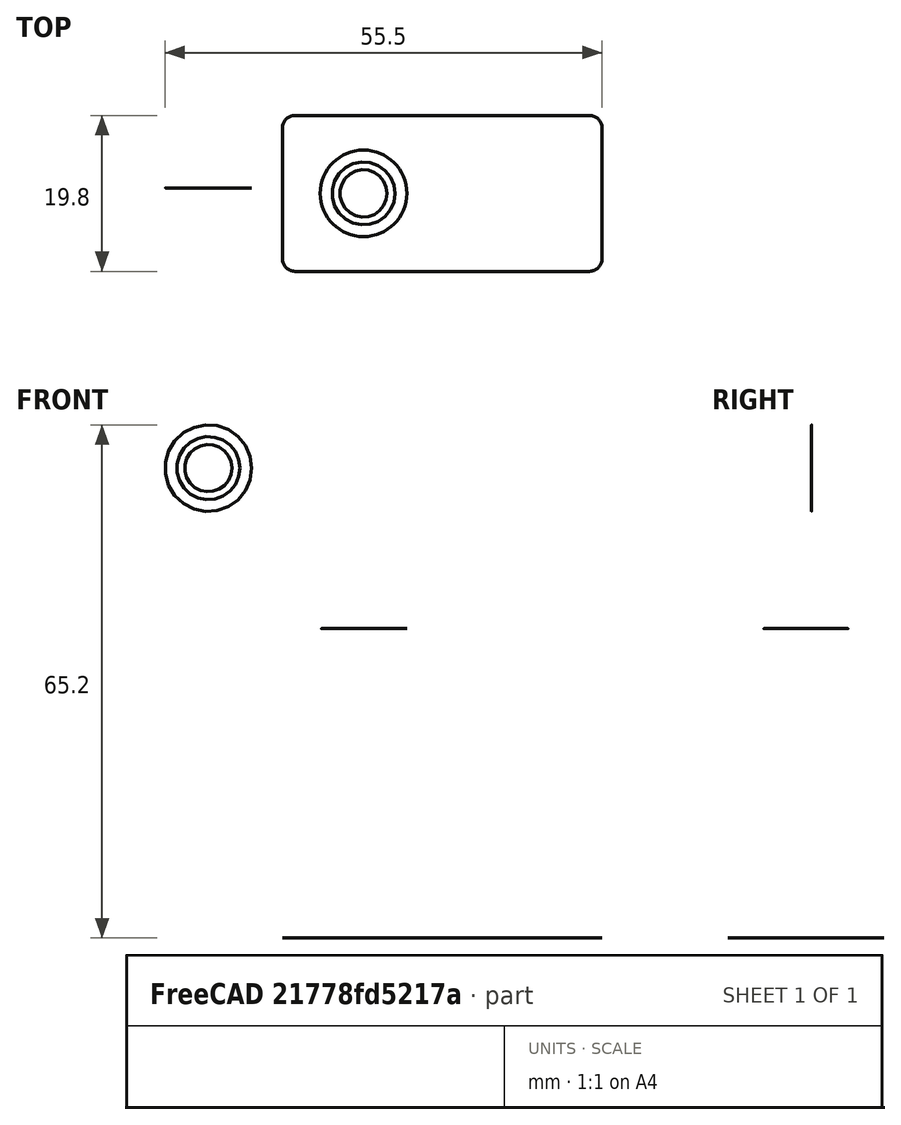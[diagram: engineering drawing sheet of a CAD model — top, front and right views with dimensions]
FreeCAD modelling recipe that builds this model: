
FCSTD DOCUMENT  (FreeCAD 2023.1102R14555 (Git shallow))
Label: Final_Assembly
License: All rights reserved
LicenseURL: https://en.wikipedia.org/wiki/All_rights_reserved
objects: App::FeaturePython×10, Part::FeaturePython×7, App::Link×3
note: 6 computed .brp shape members not serialized (recipe doc carries the construction recipe); baked Part::Feature solids carry a one-line shape summary decoded from their .brp
EXTERNAL_REF file=Base_Plate.FCStd obj=Assembly
EXTERNAL_REF file=Top_Base.FCStd obj=Assembly
EXTERNAL_REF file=Camera_Base.FCStd obj=Assembly

FEATURE [App::Link] Link  label="Link(Base_Plate_Assembly)"
  AutoLinkLabel = true
  AutoPlacement = true
  LinkedObject = -> <external Base_Plate.FCStd>#Assembly
  SyncGroupVisibility = false
  TreeRank = 1
  _LinkVersion = 1
FEATURE [App::Link] Link001  label="Link001(Top_Base_Assembly)"
  AutoLinkLabel = true
  AutoPlacement = true
  LinkPlacement = pos=(0,0,8.3) rot=(0,0,1;1.5708rad)
  LinkedObject = -> <external Top_Base.FCStd>#Assembly
  Placement = pos=(0,0,8.3) rot=(0,0,1;1.5708rad)
  SyncGroupVisibility = false
  TreeRank = 2
  _LinkVersion = 1
FEATURE [App::Link] Link002  label="Link002(Camera_Base_Assembly)"
  AutoLinkLabel = true
  AutoPlacement = true
  LinkPlacement = pos=(-19.7,-5.8,22.2) rot=(-1.2e-05,-1.2e-05,1;1.5708rad)
  LinkedObject = -> <external Camera_Base.FCStd>#Assembly
  Placement = pos=(-19.7,-5.8,22.2) rot=(-1.2e-05,-1.2e-05,1;1.5708rad)
  SyncGroupVisibility = false
  TreeRank = 16
  _LinkVersion = 1
FEATURE [Part::FeaturePython] Parts  # WARN: FeaturePython — macro-defined, semantics opaque (R4)
  Group = -> [Link,Link001,Link002]
  GroupMode = 0
  InvalidShape = false
  TreeRank = 0
  ValidateShape = false
  _LinkVersion = 1
FEATURE [Part::FeaturePython] Assembly  # WARN: FeaturePython — macro-defined, semantics opaque (R4)
  AutoRelax = true
  BuildShape = 0
  Freeze = false
  Group = -> [Constraints,Elements,Parts]
  InvalidShape = false
  TreeRank = 0
  ValidateShape = false
  Verbose = false
  _LinkVersion = 1
  _SolverType = 1
  _Version = 1
FEATURE [App::FeaturePython] Constraints  # WARN: FeaturePython — macro-defined, semantics opaque (R4)
  Group = -> [Constraint,Constraint001,Constraint002]
  TreeRank = 0
  _LinkVersion = 1
  _Version = 1
FEATURE [App::FeaturePython] Elements  # WARN: FeaturePython — macro-defined, semantics opaque (R4)
  Group = -> [_Element,_Element001,_Element002,_Element003,_Element004]
  TreeRank = 0
  _LinkVersion = 1
FEATURE [App::FeaturePython] Constraint  label="Locked"  # WARN: FeaturePython — macro-defined, semantics opaque (R4)
  Disabled = false
  Group = -> [ElementLink]
  TreeRank = 6
  _ConstraintType = 0
  _LinkVersion = 1
  _Parent = -> Constraints
FEATURE [App::FeaturePython] ElementLink  label="_Element"  # link proxy (typed FeaturePython)
  LinkTransform = true
  LinkedObject = -> _Element
  TreeRank = 4
  _LinkVersion = 1
  _Parent = -> Constraint
FEATURE [Part::FeaturePython] _Element  # link proxy (typed FeaturePython)
  Detach = false
  InvalidShape = false
  LinkTransform = true
  LinkedObject = -> Link [1.$Element.]
  TreeRank = 7
  ValidateShape = false
  _LinkVersion = 1
  _Parent = -> Elements
FEATURE [App::FeaturePython] Constraint001  label="PlaneCoincident"  # WARN: FeaturePython — macro-defined, semantics opaque (R4)
  Angle = 0
  AnglePitch = 0
  AngleRoll = 0
  Cascade = false
  Disabled = false
  Group = -> [ElementLink001,ElementLink002]
  LockAngle = true
  Multiply = false
  OffsetX = 0
  OffsetY = 0
  TreeRank = 13
  _ConstraintType = 35
  _LinkVersion = 1
  _Parent = -> Constraints
FEATURE [App::FeaturePython] ElementLink001  label="_Element001"  # link proxy (typed FeaturePython)
  LinkTransform = true
  LinkedObject = -> _Element001
  TreeRank = 9
  _LinkVersion = 1
  _Parent = -> Constraint001
FEATURE [Part::FeaturePython] _Element001  # link proxy (typed FeaturePython)
  Detach = false
  InvalidShape = false
  LinkTransform = true
  LinkedObject = -> Link [1.$Element001.]
  TreeRank = 14
  ValidateShape = false
  _LinkVersion = 1
  _Parent = -> Elements
FEATURE [App::FeaturePython] ElementLink002  label="_Element002"  # link proxy (typed FeaturePython)
  LinkTransform = true
  LinkedObject = -> _Element002
  TreeRank = 11
  _LinkVersion = 1
  _Parent = -> Constraint001
FEATURE [Part::FeaturePython] _Element002  # link proxy (typed FeaturePython)
  Detach = false
  InvalidShape = false
  LinkTransform = true
  LinkedObject = -> Link001 [1.$_Element.]
  TreeRank = 15
  ValidateShape = false
  _LinkVersion = 1
  _Parent = -> Elements
FEATURE [App::FeaturePython] Constraint002  label="PlaneCoincident001"  # WARN: FeaturePython — macro-defined, semantics opaque (R4)
  Angle = 0
  AnglePitch = 0
  AngleRoll = 18
  Cascade = false
  Disabled = false
  Group = -> [ElementLink003,ElementLink004]
  LockAngle = false
  Multiply = false
  OffsetX = 0
  OffsetY = 0
  TreeRank = 22
  _ConstraintType = 35
  _LinkVersion = 1
  _Parent = -> Constraints
FEATURE [App::FeaturePython] ElementLink003  label="Servo_Gear_Base@Link001(Top_Base_Assembly)@"  # link proxy (typed FeaturePython)
  LinkTransform = true
  LinkedObject = -> _Element003
  TreeRank = 18
  _LinkVersion = 1
  _Parent = -> Constraint002
FEATURE [Part::FeaturePython] _Element003  label="Servo_Gear_Base@Link001(Top_Base_Assembly)@"  # link proxy (typed FeaturePython)
  Detach = false
  InvalidShape = false
  LinkTransform = true
  LinkedObject = -> Link001 [1.$Servo_Gear_Base.]
  TreeRank = 23
  ValidateShape = false
  _LinkVersion = 1
  _Parent = -> Elements
FEATURE [App::FeaturePython] ElementLink004  label="Horn_Base@Link002(Camera_Base_Assembly)@"  # link proxy (typed FeaturePython)
  LinkTransform = true
  LinkedObject = -> _Element004
  TreeRank = 20
  _LinkVersion = 1
  _Parent = -> Constraint002
FEATURE [Part::FeaturePython] _Element004  label="Horn_Base@Link002(Camera_Base_Assembly)@"  # link proxy (typed FeaturePython)
  Detach = false
  InvalidShape = false
  LinkTransform = true
  LinkedObject = -> Link002 [1.$Horn_Base.]
  TreeRank = 24
  ValidateShape = false
  _LinkVersion = 1
  _Parent = -> Elements

RESOLVED EXTERNAL PARTS (link-assembly join: the EXTERNAL_REF files above that resolve inside this repo's crawl, each included once):
---- part Base_Plate.FCStd = doc fcstd_8688ca83c108 ----
FCSTD DOCUMENT  (FreeCAD 2023.1102R14555 (Git shallow))
Label: Base_Plate
License: All rights reserved
LicenseURL: https://en.wikipedia.org/wiki/All_rights_reserved
objects: Sketcher::SketchObject×11, Part::FeaturePython×7, App::FeaturePython×7, PartDesign::Pad×6, PartDesign::Pocket×6, PartDesign::Plane×5, PartDesign::Fillet×3, PartDesign::SubShapeBinder×2, PartDesign::Body×2, App::Part×2, App::Link×1
note: 82 computed .brp shape members not serialized (recipe doc carries the construction recipe); baked Part::Feature solids carry a one-line shape summary decoded from their .brp
EXTERNAL_REF file=Hitec_D625MW.FCStd obj=Part
EXTERNAL_REF file=Final_Assembly.FCStd obj=Assembly

FEATURE [App::Link] Link  label="Link(Hitec_D625MW)"
  AutoLinkLabel = true
  AutoPlacement = true
  LinkPlacement = pos=(-10.3,-9.9,-37.5) rot=(0,0,1;0rad)
  LinkedObject = -> <external Hitec_D625MW.FCStd>#Part
  Placement = pos=(-10.3,-9.9,-37.5) rot=(0,0,1;0rad)
  SyncGroupVisibility = false
  TreeRank = 1
  _LinkVersion = 1
FEATURE [Sketcher::SketchObject] Sketch
  ArcFitTolerance = 1e-06
  AttachmentSupport = -> [XY_Plane]
  ExternalBSplineMaxDegree = 5
  ExternalBSplineTolerance = 0.0001
  FullyConstrained = true
  InternalTolerance = 1e-06
  InvalidShape = false
  MakeInternals = false
  MapMode = 5
  Support = -> [XY_Plane]
  TreeRank = 21
  ValidateShape = false
  sketch-geometry (6):
    g0: LineSegment StartX=-40 StartY=-40 StartZ=0 EndX=-40 EndY=40 EndZ=0
    g1: LineSegment StartX=-40 StartY=40 StartZ=0 EndX=40 EndY=40 EndZ=0
    g2: LineSegment StartX=40 StartY=40 StartZ=0 EndX=40 EndY=-40 EndZ=0
    g3: LineSegment StartX=40 StartY=-40 StartZ=0 EndX=-40 EndY=-40 EndZ=0
    g4: GeomPoint [constr] X=0 Y=0 Z=0
    g5: Circle CenterX=0 CenterY=0 CenterZ=0 NormalX=0 NormalY=0 NormalZ=1 AngleXU=0 Radius=10
  constraints (14):
    c: Coincident(g0,g1)
    c: Coincident(g1,g2)
    c: Coincident(g2,g3)
    c: Coincident(g3,g0)
    c: Horizontal(g1)
    c: Horizontal(g3)
    c: Vertical(g0)
    c: Vertical(g2)
    c: Symmetric(g1,g0,g4)
    c: Coincident(g4,g-1)
    c: Equal(g1,g2)
    c: Distance(g1) = 80
    c: Diameter(g5) = 20
    c: Coincident(g5,g4)
FEATURE [PartDesign::Pad] Pad
  AddSubType = 0
  AlongSketchNormal = false
  AutoTaperInnerAngle = true
  CheckUpToFaceLimits = true
  ClaimChildren = false
  Direction = (0,0,1)
  Fit = 0
  FitJoin = 0
  InnerFit = 0
  InnerFitJoin = 0
  InvalidShape = false
  Length = 4
  Length2 = 10
  Linearize = true
  NewSolid = false
  Profile = -> Sketch
  ReferenceAxis = -> Sketch [N_Axis]
  Refine = true
  Suppress = false
  TaperInnerAngle = 0
  TaperInnerAngleRev = 0
  TreeRank = 22
  Type = 0
  ValidateShape = true
  _ProfileBasedVersion = 1
FEATURE [PartDesign::Fillet] Fillet
  AddSubType = 0
  Base = -> Pad [Edge1,Edge8,Edge5,Edge2]
  BaseFeature = -> Pad
  InvalidShape = false
  NewSolid = false
  Radius = 4
  Refine = true
  SupportTransform = false
  Suppress = false
  TreeRank = 23
  UseAllEdges = false
  ValidateShape = true
FEATURE [PartDesign::SubShapeBinder] Binder  label="Binder(*Hitec_D625MW)"
  BindCopyOnChange = 0
  BindMode = 0
  ClaimChildren = false
  Context = -> Assembly [Parts.Part.Body.Binder.]
  EdgeTolerance = 1e-06
  FillStyle = 0
  Fuse = false
  InvalidShape = false
  MakeFace = true
  MergeEdges = true
  OffsetFill = false
  OffsetIntersection = false
  OffsetJoinType = 0
  OffsetOpenResult = false
  Outline = false
  PartialLoad = false
  Relative = true
  SplitEdges = false
  Support = -> [Link]
  TightBound = false
  TreeRank = 39
  ValidateShape = false
  _Version = 8
FEATURE [Sketcher::SketchObject] Sketch001
  ArcFitTolerance = 1e-06
  AttachmentSupport = -> [Fillet]
  ExternalBSplineMaxDegree = 5
  ExternalBSplineTolerance = 0.0001
  ExternalGeometry = -> [Binder]
  FullyConstrained = true
  InternalTolerance = 1e-06
  InvalidShape = false
  MakeInternals = false
  MapMode = 5
  Placement = pos=(0,0,0) rot=(1,0,0;3.14159rad)
  Support = -> [Fillet]
  TreeRank = 38
  ValidateShape = false
  sketch-geometry (10):
    g0: LineSegment StartX=-17.3 StartY=11.9 StartZ=0 EndX=-10.8 EndY=11.9 EndZ=0
    g1: LineSegment StartX=-10.8 StartY=11.9 StartZ=0 EndX=-10.8 EndY=-11.9 EndZ=0
    g2: LineSegment StartX=-10.8 StartY=-11.9 StartZ=0 EndX=-17.3 EndY=-11.9 EndZ=0
    g3: LineSegment StartX=-17.3 StartY=-11.9 StartZ=0 EndX=-17.3 EndY=11.9 EndZ=0
    g4: LineSegment StartX=30.8 StartY=11.9 StartZ=0 EndX=37.3 EndY=11.9 EndZ=0
    g5: LineSegment StartX=37.3 StartY=11.9 StartZ=0 EndX=37.3 EndY=-11.9 EndZ=0
    g6: LineSegment StartX=37.3 StartY=-11.9 StartZ=0 EndX=30.8 EndY=-11.9 EndZ=0
    g7: LineSegment StartX=30.8 StartY=-11.9 StartZ=0 EndX=30.8 EndY=11.9 EndZ=0
    g8: LineSegment [constr] StartX=-15.2 StartY=9.9 StartZ=0 EndX=-15.2 EndY=11.9 EndZ=0
    g9: LineSegment [constr] StartX=-15.2 StartY=-9.9 StartZ=0 EndX=-15.2 EndY=-11.9 EndZ=0
  constraints (30):
    c: Coincident(g0,g1)
    c: Coincident(g1,g2)
    c: Coincident(g2,g3)
    c: Coincident(g3,g0)
    c: Horizontal(g0)
    c: Horizontal(g2)
    c: Vertical(g1)
    c: Vertical(g3)
    c: Coincident(g4,g5)
    c: Coincident(g5,g6)
    c: Coincident(g6,g7)
    c: Coincident(g7,g4)
    c: Horizontal(g4)
    c: Horizontal(g6)
    c: Vertical(g5)
    c: Vertical(g7)
    c: Equal(g1,g7)
    c: Equal(g0,g4)
    c: Distance(g-10,g1) = 0.5
    c: Distance(g-9,g7) = 0.5
    c: Distance(g-4,g3) = 0.5
    c: Horizontal(g4,g0)
    c: Coincident(g8,g-5)
    c: PointOnObject(g8,g0)
    c: Vertical(g8)
    c: Coincident(g9,g-3)
    c: PointOnObject(g9,g2)
    c: Vertical(g9)
    c: Equal(g9,g8)
    c: Distance(g8) = 2
FEATURE [PartDesign::Pad] Pad001
  AddSubType = 0
  AlongSketchNormal = false
  AutoTaperInnerAngle = true
  BaseFeature = -> Fillet
  CheckUpToFaceLimits = true
  ClaimChildren = false
  Direction = (0,0,-1)
  Fit = 0
  FitJoin = 0
  InnerFit = 0
  InnerFitJoin = 0
  InvalidShape = false
  Length = 10
  Length2 = 10
  Linearize = true
  NewSolid = false
  Profile = -> Sketch001
  ReferenceAxis = -> Sketch001 [N_Axis]
  Refine = true
  Suppress = false
  TaperInnerAngle = 0
  TaperInnerAngleRev = 0
  TreeRank = 40
  Type = 3
  UpToFace = -> Binder [Face2]
  ValidateShape = true
  _ProfileBasedVersion = 1
FEATURE [PartDesign::Plane] DatumPlane
  AttachmentSupport = -> [Pad001]
  InvalidShape = false
  Length = 80
  MapMode = 45
  MinimumLength = 10
  MinimumWidth = 10
  Placement = pos=(10,-1.98471e-11,-8) rot=(-0.707107,0.707107,0;3.14159rad)
  ResizeMode = 0
  Support = -> [Pad001]
  TreeRank = 41
  ValidateShape = false
  Width = 80
FEATURE [Sketcher::SketchObject] Sketch002
  ArcFitTolerance = 1e-06
  AttachmentSupport = -> [DatumPlane]
  ExternalBSplineMaxDegree = 5
  ExternalBSplineTolerance = 0.0001
  ExternalGeometry = -> [Binder,Pad001]
  FullyConstrained = true
  InternalTolerance = 1e-06
  InvalidShape = false
  MakeInternals = false
  MapMode = 5
  Placement = pos=(10,-1.98471e-11,-8) rot=(-0.707107,0.707107,0;3.14159rad)
  Support = -> [DatumPlane]
  TreeRank = 42
  ValidateShape = false
  sketch-geometry (8):
    g0: LineSegment StartX=-0.7 StartY=-20.8 StartZ=0 EndX=0.7 EndY=-20.8 EndZ=0
    g1: LineSegment StartX=0.7 StartY=-20.8 StartZ=0 EndX=0.7 EndY=-27.3 EndZ=0
    g2: LineSegment StartX=0.7 StartY=-27.3 StartZ=0 EndX=-0.7 EndY=-27.3 EndZ=0
    g3: LineSegment StartX=-0.7 StartY=-27.3 StartZ=0 EndX=-0.7 EndY=-20.8 EndZ=0
    g4: LineSegment StartX=0.7 StartY=20.8 StartZ=0 EndX=-0.7 EndY=20.8 EndZ=0
    g5: LineSegment StartX=-0.7 StartY=20.8 StartZ=0 EndX=-0.7 EndY=27.3 EndZ=0
    g6: LineSegment StartX=-0.7 StartY=27.3 StartZ=0 EndX=0.7 EndY=27.3 EndZ=0
    g7: LineSegment StartX=0.7 StartY=27.3 StartZ=0 EndX=0.7 EndY=20.8 EndZ=0
  constraints (22):
    c: Coincident(g0,g1)
    c: Coincident(g1,g2)
    c: Coincident(g2,g3)
    c: Coincident(g3,g0)
    c: Horizontal(g2)
    c: Vertical(g1)
    c: Vertical(g3)
    c: PointOnObject(g0,g-8)
    c: PointOnObject(g1,g-7)
    c: Symmetric(g0,g0,g-2)
    c: Distance(g0,g-6) = 0.1
    c: Coincident(g4,g5)
    c: Coincident(g5,g6)
    c: Coincident(g6,g7)
    c: Coincident(g7,g4)
    c: Horizontal(g6)
    c: Vertical(g5)
    c: Vertical(g7)
    c: PointOnObject(g4,g-9)
    c: PointOnObject(g5,g-10)
    c: Symmetric(g4,g4,g-2)
    c: Distance(g4,g-4) = 0.1
FEATURE [PartDesign::Pocket] Pocket
  AddSubType = 1
  AlongSketchNormal = false
  AutoTaperInnerAngle = true
  BaseFeature = -> Pad001
  CheckUpToFaceLimits = true
  ClaimChildren = false
  Direction = (0,0,1)
  Fit = 0
  FitJoin = 0
  InnerFit = 0
  InnerFitJoin = 0
  InvalidShape = false
  Length = 2.5
  Length2 = 10
  Linearize = true
  NewSolid = false
  Profile = -> Sketch002
  ReferenceAxis = -> Sketch002 [N_Axis]
  Refine = true
  Suppress = false
  TaperInnerAngle = 0
  TaperInnerAngleRev = 0
  TreeRank = 43
  Type = 0
  ValidateShape = true
  _ProfileBasedVersion = 1
  _Version = 1
FEATURE [Sketcher::SketchObject] Sketch003
  ArcFitTolerance = 1e-06
  AttachmentSupport = -> [DatumPlane]
  ExternalBSplineMaxDegree = 5
  ExternalBSplineTolerance = 0.0001
  ExternalGeometry = -> [Pocket,Binder]
  FullyConstrained = true
  InternalTolerance = 1e-06
  InvalidShape = false
  MakeInternals = false
  MapMode = 5
  Placement = pos=(10,-1.98471e-11,-8) rot=(-0.707107,0.707107,0;3.14159rad)
  Support = -> [DatumPlane]
  TreeRank = 44
  ValidateShape = false
  sketch-geometry (16):
    g0: LineSegment StartX=-11.9 StartY=-20.8 StartZ=0 EndX=-10 EndY=-20.8 EndZ=0
    g1: LineSegment StartX=-10 StartY=-20.8 StartZ=0 EndX=-10 EndY=-27.3 EndZ=0
    g2: LineSegment StartX=-10 StartY=-27.3 StartZ=0 EndX=-11.9 EndY=-27.3 EndZ=0
    g3: LineSegment StartX=-11.9 StartY=-27.3 StartZ=0 EndX=-11.9 EndY=-20.8 EndZ=0
    g4: LineSegment StartX=11.9 StartY=-20.8 StartZ=0 EndX=10 EndY=-20.8 EndZ=0
    g5: LineSegment StartX=10 StartY=-20.8 StartZ=0 EndX=10 EndY=-27.3 EndZ=0
    g6: LineSegment StartX=10 StartY=-27.3 StartZ=0 EndX=11.9 EndY=-27.3 EndZ=0
    g7: LineSegment StartX=11.9 StartY=-27.3 StartZ=0 EndX=11.9 EndY=-20.8 EndZ=0
    g8: LineSegment StartX=11.9 StartY=27.3 StartZ=0 EndX=10 EndY=27.3 EndZ=0
    g9: LineSegment StartX=10 StartY=27.3 StartZ=0 EndX=10 EndY=20.8 EndZ=0
    g10: LineSegment StartX=10 StartY=20.8 StartZ=0 EndX=11.9 EndY=20.8 EndZ=0
    g11: LineSegment StartX=11.9 StartY=20.8 StartZ=0 EndX=11.9 EndY=27.3 EndZ=0
    g12: LineSegment StartX=-11.9 StartY=27.3 StartZ=0 EndX=-10 EndY=27.3 EndZ=0
    g13: LineSegment StartX=-10 StartY=27.3 StartZ=0 EndX=-10 EndY=20.8 EndZ=0
    g14: LineSegment StartX=-10 StartY=20.8 StartZ=0 EndX=-11.9 EndY=20.8 EndZ=0
    g15: LineSegment StartX=-11.9 StartY=20.8 StartZ=0 EndX=-11.9 EndY=27.3 EndZ=0
  constraints (40):
    c: Coincident(g0,g1)
    c: Coincident(g1,g2)
    c: Coincident(g2,g3)
    c: Coincident(g3,g0)
    c: Horizontal(g0)
    c: Horizontal(g2)
    c: Vertical(g1)
    c: Coincident(g0,g-6)
    c: Coincident(g2,g-6)
    c: Coincident(g4,g5)
    c: Coincident(g5,g6)
    c: Coincident(g6,g7)
    c: Coincident(g7,g4)
    c: Horizontal(g4)
    c: Horizontal(g6)
    c: Vertical(g5)
    c: Coincident(g4,g-5)
    c: Coincident(g6,g-5)
    c: Coincident(g8,g9)
    c: Coincident(g9,g10)
    c: Coincident(g10,g11)
    c: Coincident(g11,g8)
    c: Horizontal(g8)
    c: Horizontal(g10)
    c: Vertical(g9)
    c: Coincident(g8,g-4)
    c: Coincident(g10,g-4)
    c: Coincident(g12,g13)
    c: Coincident(g13,g14)
    c: Coincident(g14,g15)
    c: Coincident(g15,g12)
    c: Horizontal(g12)
    c: Horizontal(g14)
    c: Vertical(g13)
    c: Coincident(g12,g-3)
    c: Coincident(g14,g-3)
    c: Equal(g12,g8)
    c: Equal(g8,g4)
    c: Equal(g4,g0)
    c: Distance(g-7,g13) = 0.1
FEATURE [PartDesign::Pad] Pad002
  AddSubType = 0
  AlongSketchNormal = false
  AutoTaperInnerAngle = true
  BaseFeature = -> Pocket
  CheckUpToFaceLimits = true
  ClaimChildren = false
  Direction = (0,0,-1)
  Fit = 0
  FitJoin = 0
  InnerFit = 0
  InnerFitJoin = 0
  InvalidShape = false
  Length = 2
  Length2 = 10
  Linearize = true
  NewSolid = false
  Profile = -> Sketch003
  ReferenceAxis = -> Sketch003 [N_Axis]
  Refine = true
  Suppress = false
  TaperInnerAngle = 0
  TaperInnerAngleRev = 0
  TreeRank = 45
  Type = 0
  ValidateShape = true
  _ProfileBasedVersion = 1
FEATURE [Sketcher::SketchObject] Sketch004
  ArcFitTolerance = 1e-06
  AttachmentSupport = -> [Pad002]
  ExternalBSplineMaxDegree = 5
  ExternalBSplineTolerance = 0.0001
  ExternalGeometry = -> [Binder]
  FullyConstrained = true
  InternalTolerance = 1e-06
  InvalidShape = false
  MakeInternals = false
  MapMode = 5
  Placement = pos=(0,0,4) rot=(0,0,1;0rad)
  Support = -> [Pad002]
  TreeRank = 46
  ValidateShape = false
  sketch-geometry (8):
    g0: Circle CenterX=-14.2 CenterY=5.1 CenterZ=0 NormalX=0 NormalY=0 NormalZ=1 AngleXU=0 Radius=2.3
    g1: Circle CenterX=-14.2 CenterY=-5.1 CenterZ=0 NormalX=0 NormalY=0 NormalZ=1 AngleXU=0 Radius=2.3
    g2: Circle CenterX=34.2 CenterY=5.1 CenterZ=0 NormalX=0 NormalY=0 NormalZ=1 AngleXU=0 Radius=2.3
    g3: Circle CenterX=34.2 CenterY=-5.1 CenterZ=0 NormalX=0 NormalY=0 NormalZ=1 AngleXU=0 Radius=2.3
    g4: Circle CenterX=-14.2 CenterY=5.1 CenterZ=0 NormalX=0 NormalY=0 NormalZ=1 AngleXU=0 Radius=3.75
    g5: Circle CenterX=-14.2 CenterY=-5.1 CenterZ=0 NormalX=0 NormalY=0 NormalZ=1 AngleXU=0 Radius=3.75
    g6: Circle CenterX=34.2 CenterY=5.1 CenterZ=0 NormalX=0 NormalY=0 NormalZ=1 AngleXU=0 Radius=3.75
    g7: Circle CenterX=34.2 CenterY=-5.1 CenterZ=0 NormalX=0 NormalY=0 NormalZ=1 AngleXU=0 Radius=3.75
  constraints (16):
    c: Coincident(g0,g-4)
    c: Coincident(g1,g-3)
    c: Coincident(g2,g-6)
    c: Coincident(g3,g-5)
    c: Equal(g2,g3)
    c: Equal(g3,g1)
    c: Equal(g1,g0)
    c: Diameter(g0) = 4.6
    c: Coincident(g4,g0)
    c: Coincident(g5,g1)
    c: Coincident(g6,g2)
    c: Coincident(g7,g3)
    c: Equal(g7,g6)
    c: Equal(g6,g4)
    c: Equal(g4,g5)
    c: Diameter(g5) = 7.5
FEATURE [PartDesign::Pocket] Pocket001
  AddSubType = 1
  AlongSketchNormal = false
  AutoTaperInnerAngle = true
  BaseFeature = -> Pad002
  CheckUpToFaceLimits = true
  ClaimChildren = false
  Direction = (0,0,-1)
  Fit = 0
  FitJoin = 0
  InnerFit = 0
  InnerFitJoin = 0
  InvalidShape = false
  Length = 5
  Length2 = 10
  Linearize = true
  NewSolid = false
  Profile = -> Sketch004 [Edge4,Edge3,Edge2,Edge1]
  ReferenceAxis = -> Sketch004 [N_Axis]
  Refine = true
  Suppress = false
  TaperInnerAngle = 0
  TaperInnerAngleRev = 0
  TreeRank = 47
  Type = 1
  ValidateShape = true
  _ProfileBasedVersion = 1
  _Version = 1
FEATURE [PartDesign::Pocket] Pocket002
  AddSubType = 1
  AlongSketchNormal = false
  AutoTaperInnerAngle = true
  BaseFeature = -> Pocket001
  CheckUpToFaceLimits = true
  ClaimChildren = false
  Direction = (0,0,-1)
  Fit = 0
  FitJoin = 0
  InnerFit = 0
  InnerFitJoin = 0
  InvalidShape = false
  Length = 3
  Length2 = 10
  Linearize = true
  NewSolid = false
  Profile = -> Sketch004 [Edge7,Edge8,Edge6,Edge5]
  ReferenceAxis = -> Sketch004 [N_Axis]
  Refine = true
  Suppress = false
  TaperInnerAngle = 0
  TaperInnerAngleRev = 0
  TreeRank = 48
  Type = 0
  ValidateShape = true
  _ProfileBasedVersion = 1
  _Version = 1
FEATURE [PartDesign::Body] Body
  AutoGroupSolids = false
  ClaimAllChildren = false
  ExportMode = 0
  Group = -> [Sketch,Pad,Fillet,Binder,Sketch001,Pad001,DatumPlane,Sketch002,Pocket,Sketch003,Pad002,Sketch004,Pocket001,Pocket002]
  InvalidShape = false
  Origin = -> Origin001
  Tip = -> Pocket002
  TreeRank = 19
  ValidateShape = false
  _ExportChildren = -> [Pad,Fillet,Binder,Pad001,DatumPlane,Pocket,Pad002,Pocket001,Pocket002]
  _GroupVersion = 1
FEATURE [App::Part] Part  label="Base_Plate"
  ClaimAllChildren = false
  ExportMode = 1
  Group = -> [Body]
  Origin = -> Origin
  TreeRank = 7
  _ExportChildren = -> [Body]
  _GroupVersion = 1
FEATURE [PartDesign::SubShapeBinder] Binder001  label="Binder001(*Hitec_D625MW)"
  BindCopyOnChange = 0
  BindMode = 0
  ClaimChildren = false
  Context = -> <external Final_Assembly.FCStd>#Assembly [Parts.Link.Parts.Part001.Body001.Binder001.]
  EdgeTolerance = 1e-06
  FillStyle = 0
  Fuse = false
  InvalidShape = false
  MakeFace = true
  MergeEdges = true
  OffsetFill = false
  OffsetIntersection = false
  OffsetJoinType = 0
  OffsetOpenResult = false
  Outline = false
  PartialLoad = false
  Relative = true
  SplitEdges = false
  Support = -> [Link]
  TightBound = false
  TreeRank = 68
  ValidateShape = false
  _Version = 8
FEATURE [PartDesign::Plane] DatumPlane001
  AttachmentOffset = pos=(0,0,1) rot=(0,0,1;0rad)
  AttachmentSupport = -> [Binder001]
  InvalidShape = false
  Length = 10
  MapMode = 5
  MinimumLength = 10
  MinimumWidth = 10
  Placement = pos=(0,0,-38.5) rot=(1,0,0;3.14159rad)
  ResizeMode = 0
  Support = -> [Binder001]
  TreeRank = 69
  ValidateShape = false
  Width = 10
FEATURE [Sketcher::SketchObject] Sketch005
  ArcFitTolerance = 1e-06
  AttachmentSupport = -> [DatumPlane001]
  ExternalBSplineMaxDegree = 5
  ExternalBSplineTolerance = 0.0001
  ExternalGeometry = -> [Binder001]
  FullyConstrained = true
  InternalTolerance = 1e-06
  InvalidShape = false
  MakeInternals = false
  MapMode = 5
  Placement = pos=(0,0,-38.5) rot=(1,0,0;3.14159rad)
  Support = -> [DatumPlane001]
  TreeRank = 70
  ValidateShape = false
  sketch-geometry (6):
    g0: LineSegment StartX=-43.7 StartY=-60 StartZ=0 EndX=46.3 EndY=-60 EndZ=0
    g1: LineSegment StartX=46.3 StartY=-60 StartZ=0 EndX=46.3 EndY=30 EndZ=0
    g2: LineSegment StartX=46.3 StartY=30 StartZ=0 EndX=-43.7 EndY=30 EndZ=0
    g3: LineSegment StartX=-43.7 StartY=30 StartZ=0 EndX=-43.7 EndY=-60 EndZ=0
    g4: LineSegment [constr] StartX=-8.7 StartY=9.9 StartZ=0 EndX=-43.7 EndY=9.9 EndZ=0
    g5: LineSegment [constr] StartX=28.7 StartY=9.9 StartZ=0 EndX=46.3 EndY=9.9 EndZ=0
  constraints (18):
    c: Coincident(g0,g1)
    c: Coincident(g1,g2)
    c: Coincident(g2,g3)
    c: Coincident(g3,g0)
    c: Horizontal(g0)
    c: Horizontal(g2)
    c: Vertical(g3)
    c: Equal(g1,g0)
    c: Distance(g1) = 90
    c: Coincident(g4,g-3)
    c: PointOnObject(g4,g3)
    c: Horizontal(g4)
    c: Coincident(g5,g-3)
    c: PointOnObject(g5,g1)
    c: Horizontal(g5)
    c: DistanceY(g-1,g2) = 30
    c: Vertical(g1)
    c: Distance(g4) = 35
FEATURE [PartDesign::Pad] Pad003
  AddSubType = 0
  AlongSketchNormal = false
  AutoTaperInnerAngle = true
  CheckUpToFaceLimits = true
  ClaimChildren = false
  Direction = (0,0,-1)
  Fit = 0
  FitJoin = 0
  InnerFit = 0
  InnerFitJoin = 0
  InvalidShape = false
  Length = 4
  Length2 = 10
  Linearize = true
  NewSolid = false
  Profile = -> Sketch005
  ReferenceAxis = -> Sketch005 [N_Axis]
  Refine = true
  Suppress = false
  TaperInnerAngle = 0
  TaperInnerAngleRev = 0
  TreeRank = 71
  Type = 0
  ValidateShape = true
  _ProfileBasedVersion = 1
FEATURE [Sketcher::SketchObject] Sketch006
  ArcFitTolerance = 1e-06
  AttachmentSupport = -> [Pad003]
  ExternalBSplineMaxDegree = 5
  ExternalBSplineTolerance = 0.0001
  ExternalGeometry = -> [Binder001]
  FullyConstrained = true
  InternalTolerance = 1e-06
  InvalidShape = false
  MakeInternals = false
  MapMode = 5
  Placement = pos=(0,0,-38.5) rot=(0,0,1;0rad)
  Support = -> [Pad003]
  TreeRank = 72
  ValidateShape = false
  sketch-geometry (10):
    g0: LineSegment StartX=31.3 StartY=11.9 StartZ=0 EndX=37.3 EndY=11.9 EndZ=0
    g1: LineSegment StartX=37.3 StartY=11.9 StartZ=0 EndX=37.3 EndY=-11.9 EndZ=0
    g2: LineSegment StartX=37.3 StartY=-11.9 StartZ=0 EndX=31.3 EndY=-11.9 EndZ=0
    g3: LineSegment StartX=31.3 StartY=-11.9 StartZ=0 EndX=31.3 EndY=11.9 EndZ=0
    g4: LineSegment StartX=-11.3 StartY=11.9 StartZ=0 EndX=-17.3 EndY=11.9 EndZ=0
    g5: LineSegment StartX=-17.3 StartY=11.9 StartZ=0 EndX=-17.3 EndY=-11.9 EndZ=0
    g6: LineSegment StartX=-17.3 StartY=-11.9 StartZ=0 EndX=-11.3 EndY=-11.9 EndZ=0
    g7: LineSegment StartX=-11.3 StartY=-11.9 StartZ=0 EndX=-11.3 EndY=11.9 EndZ=0
    g8: LineSegment [constr] StartX=-15.2 StartY=-9.9 StartZ=0 EndX=-15.2 EndY=-11.9 EndZ=0
    g9: LineSegment [constr] StartX=-15.2 StartY=9.9 StartZ=0 EndX=-15.2 EndY=11.9 EndZ=0
  constraints (28):
    c: Coincident(g0,g1)
    c: Coincident(g1,g2)
    c: Coincident(g2,g3)
    c: Coincident(g3,g0)
    c: Horizontal(g0)
    c: Horizontal(g2)
    c: Vertical(g3)
    c: Coincident(g4,g5)
    c: Coincident(g5,g6)
    c: Coincident(g6,g7)
    c: Coincident(g7,g4)
    c: Horizontal(g4)
    c: Horizontal(g6)
    c: Vertical(g7)
    c: Distance(g-3,g3) = 1
    c: Distance(g-4,g7) = 1
    c: Symmetric(g0,g1,g-1)
    c: Symmetric(g5,g4,g-1)
    c: Distance(g-6,g5) = 0.5
    c: Distance(g-5,g1) = 0.5
    c: Equal(g5,g1)
    c: Coincident(g8,g-7)
    c: PointOnObject(g8,g6)
    c: Vertical(g8)
    c: Coincident(g9,g-8)
    c: PointOnObject(g9,g4)
    c: Vertical(g9)
    c: Distance(g8) = 2
FEATURE [PartDesign::Pad] Pad004
  AddSubType = 0
  AlongSketchNormal = false
  AutoTaperInnerAngle = true
  BaseFeature = -> Pad003
  CheckUpToFaceLimits = true
  ClaimChildren = false
  Direction = (0,0,1)
  Fit = 0
  FitJoin = 0
  InnerFit = 0
  InnerFitJoin = 0
  InvalidShape = false
  Length = 10
  Length2 = 10
  Linearize = true
  NewSolid = false
  Profile = -> Sketch006
  ReferenceAxis = -> Sketch006 [N_Axis]
  Refine = true
  Suppress = false
  TaperInnerAngle = 0
  TaperInnerAngleRev = 0
  TreeRank = 73
  Type = 3
  UpToFace = -> Binder001 [Face37]
  ValidateShape = true
  _ProfileBasedVersion = 1
FEATURE [PartDesign::Plane] DatumPlane002
  AttachmentSupport = -> [Pad004]
  InvalidShape = false
  Length = 10
  MapMode = 45
  MinimumLength = 10
  MinimumWidth = 10
  Placement = pos=(10,-6e-16,-10.5) rot=(0,0,1;1.5708rad)
  ResizeMode = 0
  Support = -> [Pad004]
  TreeRank = 74
  ValidateShape = false
  Width = 10
FEATURE [Sketcher::SketchObject] Sketch007
  ArcFitTolerance = 1e-06
  AttachmentSupport = -> [DatumPlane002]
  ExternalBSplineMaxDegree = 5
  ExternalBSplineTolerance = 0.0001
  ExternalGeometry = -> [Pad004,Binder001]
  FullyConstrained = true
  InternalTolerance = 1e-06
  InvalidShape = false
  MakeInternals = false
  MapMode = 5
  Placement = pos=(10,-6e-16,-10.5) rot=(0,0,1;1.5708rad)
  Support = -> [DatumPlane002]
  TreeRank = 75
  ValidateShape = false
  sketch-geometry (16):
    g0: LineSegment StartX=-11.9 StartY=-21.3 StartZ=0 EndX=-10 EndY=-21.3 EndZ=0
    g1: LineSegment StartX=-10 StartY=-21.3 StartZ=0 EndX=-10 EndY=-27.3 EndZ=0
    g2: LineSegment StartX=-10 StartY=-27.3 StartZ=0 EndX=-11.9 EndY=-27.3 EndZ=0
    g3: LineSegment StartX=-11.9 StartY=-27.3 StartZ=0 EndX=-11.9 EndY=-21.3 EndZ=0
    g4: LineSegment StartX=11.9 StartY=-21.3 StartZ=0 EndX=10 EndY=-21.3 EndZ=0
    g5: LineSegment StartX=10 StartY=-21.3 StartZ=0 EndX=10 EndY=-27.3 EndZ=0
    g6: LineSegment StartX=10 StartY=-27.3 StartZ=0 EndX=11.9 EndY=-27.3 EndZ=0
    g7: LineSegment StartX=11.9 StartY=-27.3 StartZ=0 EndX=11.9 EndY=-21.3 EndZ=0
    g8: LineSegment StartX=11.9 StartY=27.3 StartZ=0 EndX=10 EndY=27.3 EndZ=0
    g9: LineSegment StartX=10 StartY=27.3 StartZ=0 EndX=10 EndY=21.3 EndZ=0
    g10: LineSegment StartX=10 StartY=21.3 StartZ=0 EndX=11.9 EndY=21.3 EndZ=0
    g11: LineSegment StartX=11.9 StartY=21.3 StartZ=0 EndX=11.9 EndY=27.3 EndZ=0
    g12: LineSegment StartX=-11.9 StartY=27.3 StartZ=0 EndX=-10 EndY=27.3 EndZ=0
    g13: LineSegment StartX=-10 StartY=27.3 StartZ=0 EndX=-10 EndY=21.3 EndZ=0
    g14: LineSegment StartX=-10 StartY=21.3 StartZ=0 EndX=-11.9 EndY=21.3 EndZ=0
    g15: LineSegment StartX=-11.9 StartY=21.3 StartZ=0 EndX=-11.9 EndY=27.3 EndZ=0
  constraints (40):
    c: Coincident(g0,g1)
    c: Coincident(g1,g2)
    c: Coincident(g2,g3)
    c: Coincident(g3,g0)
    c: Horizontal(g0)
    c: Horizontal(g2)
    c: Vertical(g1)
    c: Coincident(g0,g-6)
    c: Coincident(g4,g5)
    c: Coincident(g5,g6)
    c: Coincident(g6,g7)
    c: Coincident(g7,g4)
    c: Horizontal(g4)
    c: Horizontal(g6)
    c: Vertical(g5)
    c: Coincident(g4,g-5)
    c: Coincident(g8,g9)
    c: Coincident(g9,g10)
    c: Coincident(g10,g11)
    c: Coincident(g11,g8)
    c: Horizontal(g8)
    c: Horizontal(g10)
    c: Vertical(g9)
    c: Coincident(g8,g-4)
    c: Coincident(g12,g13)
    c: Coincident(g13,g14)
    c: Coincident(g14,g15)
    c: Coincident(g15,g12)
    c: Horizontal(g12)
    c: Horizontal(g14)
    c: Vertical(g13)
    c: Coincident(g12,g-3)
    c: Coincident(g14,g-3)
    c: Coincident(g2,g-6)
    c: Coincident(g6,g-5)
    c: Coincident(g10,g-4)
    c: Equal(g8,g12)
    c: Equal(g12,g2)
    c: Equal(g2,g6)
    c: Distance(g9,g-7) = 0.1
FEATURE [PartDesign::Pad] Pad005
  AddSubType = 0
  AlongSketchNormal = false
  AutoTaperInnerAngle = true
  BaseFeature = -> Pad004
  CheckUpToFaceLimits = true
  ClaimChildren = false
  Direction = (-1e-16,0,1)
  Fit = 0
  FitJoin = 0
  InnerFit = 0
  InnerFitJoin = 0
  InvalidShape = false
  Length = 2
  Length2 = 10
  Linearize = true
  NewSolid = false
  Profile = -> Sketch007
  ReferenceAxis = -> Sketch007 [N_Axis]
  Refine = true
  Suppress = false
  TaperInnerAngle = 0
  TaperInnerAngleRev = 0
  TreeRank = 76
  Type = 0
  ValidateShape = true
  _ProfileBasedVersion = 1
FEATURE [Sketcher::SketchObject] Sketch008
  ArcFitTolerance = 1e-06
  AttachmentSupport = -> [DatumPlane002]
  ExternalBSplineMaxDegree = 5
  ExternalBSplineTolerance = 0.0001
  ExternalGeometry = -> [Binder001]
  FullyConstrained = true
  InternalTolerance = 1e-06
  InvalidShape = false
  MakeInternals = false
  MapMode = 5
  Placement = pos=(10,-6e-16,-10.5) rot=(0,0,1;1.5708rad)
  Support = -> [DatumPlane002]
  TreeRank = 77
  ValidateShape = false
  sketch-geometry (4):
    g0: Circle CenterX=-5.1 CenterY=24.2 CenterZ=0 NormalX=0 NormalY=0 NormalZ=1 AngleXU=0 Radius=2.3
    g1: Circle CenterX=5.1 CenterY=24.2 CenterZ=0 NormalX=0 NormalY=0 NormalZ=1 AngleXU=0 Radius=2.3
    g2: Circle CenterX=-5.1 CenterY=-24.2 CenterZ=0 NormalX=0 NormalY=0 NormalZ=1 AngleXU=0 Radius=2.3
    g3: Circle CenterX=5.1 CenterY=-24.2 CenterZ=0 NormalX=0 NormalY=0 NormalZ=1 AngleXU=0 Radius=2.3
  constraints (8):
    c: Coincident(g0,g-5)
    c: Coincident(g1,g-6)
    c: Coincident(g2,g-3)
    c: Coincident(g3,g-4)
    c: Equal(g3,g2)
    c: Equal(g2,g0)
    c: Equal(g0,g1)
    c: Diameter(g2) = 4.6
FEATURE [PartDesign::Pocket] Pocket003
  AddSubType = 1
  AlongSketchNormal = false
  AutoTaperInnerAngle = true
  BaseFeature = -> Pad005
  CheckUpToFaceLimits = true
  ClaimChildren = false
  Direction = (1e-16,0,-1)
  Fit = 0
  FitJoin = 0
  InnerFit = 0
  InnerFitJoin = 0
  InvalidShape = false
  Length = 17
  Length2 = 10
  Linearize = true
  NewSolid = false
  Profile = -> Sketch008
  ReferenceAxis = -> Sketch008 [N_Axis]
  Refine = true
  Suppress = false
  TaperInnerAngle = 0
  TaperInnerAngleRev = 0
  TreeRank = 78
  Type = 0
  ValidateShape = true
  _ProfileBasedVersion = 1
  _Version = 1
FEATURE [PartDesign::Plane] DatumPlane003
  AttachmentOffset = pos=(0,0,0) rot=(1,0,0;1.5708rad)
  AttachmentSupport = -> [Pocket003]
  InvalidShape = false
  Length = 24.3309
  MapMode = 45
  MinimumLength = 10
  MinimumWidth = 10
  Placement = pos=(10,4e-16,-24.3309) rot=(0,1,0;4.71239rad)
  ResizeMode = 0
  Support = -> [Pocket003]
  TreeRank = 79
  ValidateShape = false
  Width = 10
FEATURE [Sketcher::SketchObject] Sketch009
  ArcFitTolerance = 1e-06
  AttachmentSupport = -> [DatumPlane003]
  ExternalBSplineMaxDegree = 5
  ExternalBSplineTolerance = 0.0001
  ExternalGeometry = -> [Pocket003,Binder001]
  FullyConstrained = true
  InternalTolerance = 1e-06
  InvalidShape = false
  MakeInternals = false
  MapMode = 5
  Placement = pos=(10,4e-16,-24.3309) rot=(0,-1,0;1.5708rad)
  Support = -> [DatumPlane003]
  TreeRank = 80
  ValidateShape = false
  sketch-geometry (11):
    g0: GeomPoint [constr] X=13.8309 Y=5.1 Z=0
    g1: GeomPoint [constr] X=13.8309 Y=-5.1 Z=0
    g2: LineSegment StartX=7.83086 StartY=-8.65 StartZ=0 EndX=4.53086 EndY=-8.65 EndZ=0
    g3: LineSegment StartX=4.53086 StartY=-8.65 StartZ=0 EndX=4.53086 EndY=-1.55 EndZ=0
    g4: LineSegment StartX=4.53086 StartY=-1.55 StartZ=0 EndX=7.83086 EndY=-1.55 EndZ=0
    g5: LineSegment StartX=7.83086 StartY=-1.55 StartZ=0 EndX=7.83086 EndY=-8.65 EndZ=0
    g6: LineSegment StartX=7.83086 StartY=1.55 StartZ=0 EndX=4.53086 EndY=1.55 EndZ=0
    g7: LineSegment StartX=4.53086 StartY=1.55 StartZ=0 EndX=4.53086 EndY=8.65 EndZ=0
    g8: LineSegment StartX=4.53086 StartY=8.65 StartZ=0 EndX=7.83086 EndY=8.65 EndZ=0
    g9: LineSegment StartX=7.83086 StartY=8.65 StartZ=0 EndX=7.83086 EndY=1.55 EndZ=0
    g10: LineSegment [constr] StartX=13.8309 StartY=-5.1 StartZ=0 EndX=7.83086 EndY=-5.1 EndZ=0
  constraints (27):
    c: Symmetric(g-4,g-5,g1)
    c: Symmetric(g-6,g-7,g0)
    c: Coincident(g2,g3)
    c: Coincident(g3,g4)
    c: Coincident(g4,g5)
    c: Coincident(g5,g2)
    c: Horizontal(g2)
    c: Horizontal(g4)
    c: Vertical(g3)
    c: Vertical(g5)
    c: Coincident(g6,g7)
    c: Coincident(g7,g8)
    c: Coincident(g8,g9)
    c: Coincident(g9,g6)
    c: Horizontal(g6)
    c: Horizontal(g8)
    c: Vertical(g7)
    c: Vertical(g9)
    c: Equal(g5,g9)
    c: Equal(g4,g6)
    c: Symmetric(g4,g6,g-1)
    c: Distance(g3) = 7.1
    c: Distance(g2) = 3.3
    c: Coincident(g10,g1)
    c: Horizontal(g10)
    c: Symmetric(g4,g2,g10)
    c: Distance(g10) = 6
FEATURE [PartDesign::Pocket] Pocket004
  AddSubType = 1
  AlongSketchNormal = false
  AutoTaperInnerAngle = true
  BaseFeature = -> Pocket003
  CheckUpToFaceLimits = true
  ClaimChildren = false
  Direction = (1,6.04e-14,1.848e-13)
  Fit = 0
  FitJoin = 0
  InnerFit = 0
  InnerFitJoin = 0
  InvalidShape = false
  Length = 5
  Length2 = 10
  Linearize = true
  Midplane = true
  NewSolid = false
  Profile = -> Sketch009
  ReferenceAxis = -> Sketch009 [N_Axis]
  Refine = true
  Suppress = false
  TaperInnerAngle = 0
  TaperInnerAngleRev = 0
  TreeRank = 81
  Type = 1
  ValidateShape = true
  _ProfileBasedVersion = 1
  _Version = 1
FEATURE [PartDesign::Plane] DatumPlane004
  AttachmentSupport = -> [Pocket004]
  InvalidShape = false
  Length = 19.8
  MapMode = 5
  MinimumLength = 10
  MinimumWidth = 10
  Placement = pos=(-11.3,0,0) rot=(0.57735,0.57735,0.57735;2.0944rad)
  ResizeMode = 0
  Support = -> [Pocket004]
  TreeRank = 82
  ValidateShape = false
  Width = 43.3
FEATURE [Sketcher::SketchObject] Sketch010
  ArcFitTolerance = 1e-06
  AttachmentSupport = -> [DatumPlane004]
  ExternalBSplineMaxDegree = 5
  ExternalBSplineTolerance = 0.0001
  ExternalGeometry = -> [Binder001]
  FullyConstrained = true
  InternalTolerance = 1e-06
  InvalidShape = false
  MakeInternals = false
  MapMode = 5
  Placement = pos=(-11.3,0,0) rot=(0.57735,0.57735,0.57735;2.0944rad)
  Support = -> [DatumPlane004]
  TreeRank = 83
  ValidateShape = false
  sketch-geometry (7):
    g0: LineSegment StartX=4.95 StartY=-35.9 StartZ=0 EndX=4.95 EndY=-28.7 EndZ=0
    g1: LineSegment StartX=4.95 StartY=-28.7 StartZ=0 EndX=-4.95 EndY=-28.7 EndZ=0
    g2: LineSegment StartX=-4.95 StartY=-28.7 StartZ=0 EndX=-4.95 EndY=-35.9 EndZ=0
    g3: LineSegment StartX=-4.95 StartY=-35.9 StartZ=0 EndX=4.95 EndY=-35.9 EndZ=0
    g4: GeomPoint [constr] X=0 Y=-32.3 Z=0
    g5: LineSegment [constr] StartX=-4.95 StartY=-28.7 StartZ=0 EndX=-3.45 EndY=-30.2 EndZ=0
    g6: LineSegment [constr] StartX=-4.95 StartY=-35.9 StartZ=0 EndX=-3.45 EndY=-34.4 EndZ=0
  constraints (17):
    c: Coincident(g0,g1)
    c: Coincident(g1,g2)
    c: Coincident(g2,g3)
    c: Coincident(g3,g0)
    c: Horizontal(g1)
    c: Horizontal(g3)
    c: Vertical(g0)
    c: Vertical(g2)
    c: Symmetric(g1,g0,g4)
    c: PointOnObject(g4,g-2)
    c: Coincident(g5,g1)
    c: Coincident(g5,g-4)
    c: Angle(g5,g1) = 0.785398
    c: Distance(g-4,g2) = 1.5
    c: Coincident(g6,g2)
    c: Coincident(g6,g-4)
    c: Angle(g3,g6) = 0.785398
FEATURE [PartDesign::Pocket] Pocket005
  AddSubType = 1
  AlongSketchNormal = false
  AutoTaperInnerAngle = true
  BaseFeature = -> Pocket004
  CheckUpToFaceLimits = true
  ClaimChildren = false
  Direction = (-1,0,0)
  Fit = 0
  FitJoin = 0
  InnerFit = 0
  InnerFitJoin = 0
  InvalidShape = false
  Length = 10
  Length2 = 10
  Linearize = true
  NewSolid = false
  Profile = -> Sketch010
  ReferenceAxis = -> Sketch010 [N_Axis]
  Refine = true
  Suppress = false
  TaperInnerAngle = 0
  TaperInnerAngleRev = 0
  TreeRank = 84
  Type = 0
  ValidateShape = true
  _ProfileBasedVersion = 1
  _Version = 1
FEATURE [PartDesign::Fillet] Fillet001
  AddSubType = 0
  Base = -> Pocket005 [Edge105,Edge108,Edge107,Edge106]
  BaseFeature = -> Pocket005
  InvalidShape = false
  NewSolid = false
  Radius = 1
  Refine = true
  SupportTransform = false
  Suppress = false
  TreeRank = 85
  UseAllEdges = false
  ValidateShape = true
FEATURE [PartDesign::Fillet] Fillet002
  AddSubType = 0
  Base = -> Fillet001 [Edge92,Edge90,Edge88,Edge87]
  BaseFeature = -> Fillet001
  InvalidShape = false
  NewSolid = false
  Radius = 4
  Refine = true
  SupportTransform = false
  Suppress = false
  TreeRank = 86
  UseAllEdges = false
  ValidateShape = true
FEATURE [PartDesign::Body] Body001
  AutoGroupSolids = false
  ClaimAllChildren = false
  ExportMode = 0
  Group = -> [Binder001,DatumPlane001,Sketch005,Pad003,Sketch006,Pad004,DatumPlane002,Sketch007,Pad005,Sketch008,Pocket003,DatumPlane003,Sketch009,Pocket004,DatumPlane004,Sketch010,Pocket005,Fillet001,Fillet002]
  InvalidShape = false
  Origin = -> Origin003
  Tip = -> Fillet002
  TreeRank = 67
  ValidateShape = false
  _ExportChildren = -> [Binder001,DatumPlane001,Pad003,Pad004,DatumPlane002,Pad005,Pocket003,DatumPlane003,Pocket004,DatumPlane004,Pocket005,Fillet001,Fillet002]
  _GroupVersion = 1
FEATURE [App::Part] Part001  label="Base_Plate_V2"
  ClaimAllChildren = false
  ExportMode = 1
  Group = -> [Body001]
  Origin = -> Origin002
  TreeRank = 55
  _ExportChildren = -> [Body001]
  _GroupVersion = 1
FEATURE [Part::FeaturePython] Parts  # WARN: FeaturePython — macro-defined, semantics opaque (R4)
  Group = -> [Part,Part001,Link]
  GroupMode = 0
  InvalidShape = false
  TreeRank = 0
  ValidateShape = false
  _LinkVersion = 1
FEATURE [Part::FeaturePython] Assembly  label="Base_Plate_Assembly"  # WARN: FeaturePython — macro-defined, semantics opaque (R4)
  AutoRelax = true
  BuildShape = 0
  Freeze = false
  Group = -> [Constraints,Elements,Parts]
  InvalidShape = false
  TreeRank = 2
  ValidateShape = false
  Verbose = false
  _LinkVersion = 1
  _SolverType = 1
  _Version = 1
FEATURE [App::FeaturePython] Constraints  # WARN: FeaturePython — macro-defined, semantics opaque (R4)
  Group = -> [Constraint,Constraint001]
  TreeRank = 0
  _LinkVersion = 1
  _Version = 1
FEATURE [App::FeaturePython] Elements  # WARN: FeaturePython — macro-defined, semantics opaque (R4)
  Group = -> [_Element,_Element001,_Element002,Element,Element001]
  TreeRank = 0
  _LinkVersion = 1
FEATURE [App::FeaturePython] Constraint  label="Locked"  # WARN: FeaturePython — macro-defined, semantics opaque (R4)
  Disabled = false
  Group = -> [ElementLink]
  TreeRank = 27
  _ConstraintType = 0
  _LinkVersion = 1
  _Parent = -> Constraints
FEATURE [App::FeaturePython] ElementLink  label="_Element"  # link proxy (typed FeaturePython)
  LinkTransform = true
  LinkedObject = -> _Element
  TreeRank = 25
  _LinkVersion = 1
  _Parent = -> Constraint
FEATURE [Part::FeaturePython] _Element  # link proxy (typed FeaturePython)
  Detach = false
  InvalidShape = false
  LinkTransform = true
  LinkedObject = -> Part [Body.Fillet.Face2]
  TreeRank = 28
  ValidateShape = false
  _LinkVersion = 1
  _Parent = -> Elements
FEATURE [App::FeaturePython] Constraint001  label="Attachment"  # WARN: FeaturePython — macro-defined, semantics opaque (R4)
  Cascade = false
  Disabled = false
  Group = -> [ElementLink001,ElementLink002]
  Multiply = false
  TreeRank = 34
  _ConstraintType = 45
  _LinkVersion = 1
  _Parent = -> Constraints
FEATURE [App::FeaturePython] ElementLink001  label="_Element001"  # link proxy (typed FeaturePython)
  LinkTransform = true
  LinkedObject = -> _Element001
  TreeRank = 30
  _LinkVersion = 1
  _Parent = -> Constraint001
FEATURE [Part::FeaturePython] _Element001  # link proxy (typed FeaturePython)
  Detach = false
  InvalidShape = false
  LinkTransform = true
  LinkedObject = -> Link [Body.Fillet.Edge169]
  TreeRank = 35
  ValidateShape = false
  _LinkVersion = 1
  _Parent = -> Elements
FEATURE [App::FeaturePython] ElementLink002  label="_Element002"  # link proxy (typed FeaturePython)
  LinkTransform = true
  LinkedObject = -> _Element002
  TreeRank = 32
  _LinkVersion = 1
  _Parent = -> Constraint001
FEATURE [Part::FeaturePython] _Element002  # link proxy (typed FeaturePython)
  Detach = false
  InvalidShape = false
  LinkTransform = true
  LinkedObject = -> Part [Body.Fillet.Edge12]
  TreeRank = 36
  ValidateShape = false
  _LinkVersion = 1
  _Parent = -> Elements
FEATURE [Part::FeaturePython] Element  # link proxy (typed FeaturePython)
  Detach = false
  InvalidShape = false
  LinkTransform = true
  LinkedObject = -> Link [Body.Fillet.Face34]
  TreeRank = 49
  ValidateShape = false
  _LinkVersion = 1
  _Parent = -> Elements
FEATURE [Part::FeaturePython] Element001  # link proxy (typed FeaturePython)
  Detach = false
  InvalidShape = false
  LinkTransform = true
  LinkedObject = -> Link [Body.Fillet.Face63]
  TreeRank = 50
  ValidateShape = false
  _LinkVersion = 1
  _Parent = -> Elements
---- part Camera_Base.FCStd = doc fcstd_c71ad3286b8e ----
FCSTD DOCUMENT  (FreeCAD 2023.1102R14555 (Git shallow))
Label: Camera_Base
License: All rights reserved
LicenseURL: https://en.wikipedia.org/wiki/All_rights_reserved
objects: App::FeaturePython×8, Part::FeaturePython×7, Sketcher::SketchObject×3, App::Link×2, PartDesign::SubShapeBinder×2, Part::SubShapeBinder×2, PartDesign::Pocket×2, PartDesign::Plane×1, PartDesign::Pad×1, PartDesign::Fillet×1, PartDesign::Body×1, App::Part×1
note: 30 computed .brp shape members not serialized (recipe doc carries the construction recipe); baked Part::Feature solids carry a one-line shape summary decoded from their .brp
EXTERNAL_REF file=Servo_Horn.FCStd obj=Part
EXTERNAL_REF file=Camera_Holder.FCStd obj=Assembly
EXTERNAL_REF file=Final_Assembly.FCStd obj=Assembly

FEATURE [App::Link] Link  label="Link(Servo_Horn)"
  AutoLinkLabel = true
  AutoPlacement = true
  LinkPlacement = pos=(0,0,0) rot=(-0.57735,0.57735,-0.57735;2.0944rad)
  LinkedObject = -> <external Servo_Horn.FCStd>#Part
  Placement = pos=(0,0,0) rot=(-0.57735,0.57735,-0.57735;2.0944rad)
  SyncGroupVisibility = false
  TreeRank = 1
  _LinkVersion = 1
FEATURE [PartDesign::SubShapeBinder] Binder  label="Binder(Pocket)"
  BindCopyOnChange = 0
  BindMode = 0
  ClaimChildren = false
  Context = -> Assembly [Parts.Part.Binder.]
  EdgeTolerance = 1e-06
  FillStyle = 0
  Fuse = false
  InvalidShape = false
  MakeFace = true
  MergeEdges = true
  OffsetFill = false
  OffsetIntersection = false
  OffsetJoinType = 0
  OffsetOpenResult = false
  Outline = false
  PartialLoad = false
  Relative = true
  SplitEdges = false
  Support = -> [Link[Body.Pocket.Face9]]
  TightBound = false
  TreeRank = 7
  ValidateShape = false
  _Version = 8
FEATURE [PartDesign::Plane] DatumPlane
  AttachmentOffset = pos=(0,0,0) rot=(1,0,0;1.5708rad)
  AttachmentSupport = -> [Binder]
  InvalidShape = false
  Length = 50
  MapMode = 5
  MinimumLength = 10
  MinimumWidth = 10
  Placement = pos=(0,0,0) rot=(-0.707107,0.707107,0;3.14159rad)
  ResizeMode = 0
  Support = -> [Binder]
  TreeRank = 8
  ValidateShape = false
  Width = 50
FEATURE [Part::SubShapeBinder] Import  label="Import(DatumPlane)"
  BindCopyOnChange = 0
  BindMode = 0
  ClaimChildren = false
  Context = -> Assembly [Parts.Part.Body.Import.]
  EdgeTolerance = 1e-06
  FillStyle = 0
  Fuse = false
  InvalidShape = false
  MakeFace = false
  MergeEdges = true
  OffsetFill = false
  OffsetIntersection = false
  OffsetJoinType = 0
  OffsetOpenResult = false
  Outline = false
  PartialLoad = false
  Relative = true
  SplitEdges = false
  Support = -> [DatumPlane]
  TightBound = false
  TreeRank = 23
  ValidateShape = false
  _Version = 8
FEATURE [Sketcher::SketchObject] Sketch
  ArcFitTolerance = 1e-06
  AttachmentSupport = -> [Import]
  ExternalBSplineMaxDegree = 5
  ExternalBSplineTolerance = 0.0001
  FullyConstrained = true
  InternalTolerance = 1e-06
  InvalidShape = false
  MakeInternals = false
  MapMode = 5
  Placement = pos=(0,0,0) rot=(1,0,0;3.14159rad)
  Support = -> [Import]
  TreeRank = 24
  ValidateShape = false
  sketch-geometry (8):
    g0: LineSegment StartX=0 StartY=20 StartZ=0 EndX=-50 EndY=20 EndZ=0
    g1: LineSegment StartX=-50 StartY=20 StartZ=0 EndX=-50 EndY=-25 EndZ=0
    g2: LineSegment StartX=-50 StartY=-25 StartZ=0 EndX=0 EndY=-25 EndZ=0
    g3: LineSegment StartX=0 StartY=-25 StartZ=0 EndX=0 EndY=20 EndZ=0
    g4: LineSegment StartX=-15 StartY=12.5 StartZ=0 EndX=-5 EndY=12.5 EndZ=0
    g5: LineSegment StartX=-5 StartY=12.5 StartZ=0 EndX=-5 EndY=-12.5 EndZ=0
    g6: LineSegment StartX=-5 StartY=-12.5 StartZ=0 EndX=-15 EndY=-12.5 EndZ=0
    g7: LineSegment StartX=-15 StartY=-12.5 StartZ=0 EndX=-15 EndY=12.5 EndZ=0
  constraints (23):
    c: Coincident(g0,g1)
    c: Coincident(g1,g2)
    c: Coincident(g2,g3)
    c: Coincident(g3,g0)
    c: Horizontal(g0)
    c: Horizontal(g2)
    c: Vertical(g1)
    c: Vertical(g3)
    c: Distance(g0) = 50
    c: Coincident(g4,g5)
    c: Coincident(g5,g6)
    c: Coincident(g6,g7)
    c: Coincident(g7,g4)
    c: Horizontal(g4)
    c: Horizontal(g6)
    c: Vertical(g7)
    c: Symmetric(g4,g5,g-1)
    c: Distance(g4,g3) = 5
    c: Distance(g7) = 25
    c: Distance(g4) = 10
    c: PointOnObject(g0,g-2)
    c: DistanceY(g2,g-1) = 25
    c: DistanceY(g-1,g0) = 20
FEATURE [PartDesign::Pad] Pad
  AddSubType = 0
  AlongSketchNormal = false
  AutoTaperInnerAngle = true
  CheckUpToFaceLimits = true
  ClaimChildren = false
  Direction = (-1.19209e-07,2e-16,-1)
  Fit = 0
  FitJoin = 0
  InnerFit = 0
  InnerFitJoin = 0
  InvalidShape = false
  Length = 7
  Length2 = 10
  Linearize = true
  Midplane = true
  NewSolid = false
  Profile = -> Sketch
  ReferenceAxis = -> Sketch [N_Axis]
  Refine = true
  Suppress = false
  TaperInnerAngle = 0
  TaperInnerAngleRev = 0
  TreeRank = 25
  Type = 0
  ValidateShape = true
  _ProfileBasedVersion = 1
FEATURE [Part::SubShapeBinder] Import001  label="Import001(*Pocket)"
  BindCopyOnChange = 0
  BindMode = 0
  ClaimChildren = false
  Context = -> Assembly [Parts.Part.Body.Import001.]
  EdgeTolerance = 1e-06
  FillStyle = 0
  Fuse = false
  InvalidShape = false
  MakeFace = false
  MergeEdges = true
  OffsetFill = false
  OffsetIntersection = false
  OffsetJoinType = 0
  OffsetOpenResult = false
  Outline = false
  PartialLoad = false
  Relative = true
  SplitEdges = false
  Support = -> [Binder]
  TightBound = false
  TreeRank = 27
  ValidateShape = false
  _Version = 8
FEATURE [Sketcher::SketchObject] Sketch001
  ArcFitTolerance = 1e-06
  AttachmentSupport = -> [Pad]
  ExternalBSplineMaxDegree = 5
  ExternalBSplineTolerance = 0.0001
  ExternalGeometry = -> [Import001]
  FullyConstrained = true
  InternalTolerance = 1e-06
  InvalidShape = false
  MakeInternals = false
  MapMode = 5
  Placement = pos=(0,0,0) rot=(0.57735,0.57735,0.57735;2.0944rad)
  Support = -> [Pad]
  TreeRank = 26
  ValidateShape = false
  sketch-geometry (2):
    g0: Circle CenterX=-7 CenterY=0 CenterZ=0 NormalX=0 NormalY=0 NormalZ=1 AngleXU=0 Radius=2.1
    g1: Circle CenterX=7 CenterY=0 CenterZ=0 NormalX=0 NormalY=0 NormalZ=1 AngleXU=0 Radius=2.1
  constraints (4):
    c: Coincident(g0,g-3)
    c: Coincident(g1,g-4)
    c: Equal(g1,g0)
    c: Diameter(g0) = 4.2
FEATURE [PartDesign::Pocket] Pocket
  AddSubType = 1
  AlongSketchNormal = false
  AutoTaperInnerAngle = true
  BaseFeature = -> Pad
  CheckUpToFaceLimits = true
  ClaimChildren = false
  Direction = (-1,0,1.19209e-07)
  Fit = 0
  FitJoin = 0
  InnerFit = 0
  InnerFitJoin = 0
  InvalidShape = false
  Length = 8
  Length2 = 10
  Linearize = true
  NewSolid = false
  Profile = -> Sketch001
  ReferenceAxis = -> Sketch001 [N_Axis]
  Refine = true
  Suppress = false
  TaperInnerAngle = 0
  TaperInnerAngleRev = 0
  TreeRank = 28
  Type = 0
  ValidateShape = true
  _ProfileBasedVersion = 1
  _Version = 1
FEATURE [PartDesign::Fillet] Fillet
  AddSubType = 0
  Base = -> Pocket [Edge2,Edge1,Edge5,Edge11,Edge33,Edge32,Edge31,Edge30]
  BaseFeature = -> Pocket
  InvalidShape = false
  NewSolid = false
  Radius = 2
  Refine = true
  SupportTransform = false
  Suppress = false
  TreeRank = 30
  UseAllEdges = false
  ValidateShape = true
FEATURE [App::Link] Link001  label="Link001(Camera_Holder_Assembly)"
  AutoLinkLabel = true
  AutoPlacement = true
  LinkPlacement = pos=(-30,21,27) rot=(1,0,0;1.5708rad)
  LinkedObject = -> <external Camera_Holder.FCStd>#Assembly
  Placement = pos=(-30,21,27) rot=(1,0,0;1.5708rad)
  SyncGroupVisibility = false
  TreeRank = 31
  _LinkVersion = 1
FEATURE [PartDesign::SubShapeBinder] Binder001  label="Binder001(Fillet001)..."
  BindCopyOnChange = 0
  BindMode = 0
  ClaimChildren = false
  Context = -> <external Final_Assembly.FCStd>#Assembly [Parts.Link002.Parts.Part.Body.Binder001.]
  EdgeTolerance = 1e-06
  FillStyle = 0
  Fuse = false
  InvalidShape = false
  MakeFace = true
  MergeEdges = true
  OffsetFill = false
  OffsetIntersection = false
  OffsetJoinType = 0
  OffsetOpenResult = false
  Outline = false
  PartialLoad = false
  Relative = true
  SplitEdges = false
  Support = -> [Link001[Parts.Part.Body.Fillet001.Edge43,Parts.Part.Body.Fillet001.Edge42]]
  TightBound = false
  TreeRank = 32
  ValidateShape = false
  _Version = 8
FEATURE [Sketcher::SketchObject] Sketch002
  ArcFitTolerance = 1e-06
  AttachmentSupport = -> [Fillet]
  ExternalBSplineMaxDegree = 5
  ExternalBSplineTolerance = 0.0001
  ExternalGeometry = -> [Binder001]
  FullyConstrained = true
  InternalTolerance = 1e-06
  InvalidShape = false
  MakeInternals = false
  MapMode = 5
  Placement = pos=(4.17233e-07,-7e-16,3.5) rot=(0,1,0;0rad)
  Support = -> [Fillet]
  TreeRank = 33
  ValidateShape = false
FEATURE [PartDesign::Pocket] Pocket001
  AddSubType = 1
  AlongSketchNormal = false
  AutoTaperInnerAngle = true
  BaseFeature = -> Fillet
  CheckUpToFaceLimits = true
  ClaimChildren = false
  Direction = (-1.19209e-07,2e-16,-1)
  Fit = 0
  FitJoin = 0
  InnerFit = 0
  InnerFitJoin = 0
  InvalidShape = false
  Length = 8
  Length2 = 10
  Linearize = true
  NewSolid = false
  Profile = -> Sketch002
  ReferenceAxis = -> Sketch002 [N_Axis]
  Refine = true
  Suppress = false
  TaperInnerAngle = 0
  TaperInnerAngleRev = 0
  TreeRank = 34
  Type = 0
  ValidateShape = true
  _ProfileBasedVersion = 1
  _Version = 1
FEATURE [PartDesign::Body] Body
  AutoGroupSolids = false
  ClaimAllChildren = false
  ExportMode = 0
  Group = -> [Import,Sketch,Pad,Sketch001,Import001,Pocket,Fillet,Binder001,Sketch002,Pocket001]
  InvalidShape = false
  Origin = -> Origin001
  Tip = -> Pocket001
  TreeRank = 20
  ValidateShape = false
  _ExportChildren = -> [Import,Pad,Import001,Pocket,Fillet,Binder001,Pocket001]
  _GroupVersion = 1
FEATURE [App::Part] Part
  ClaimAllChildren = false
  ExportMode = 1
  Group = -> [Binder,DatumPlane,Body]
  Origin = -> Origin
  TreeRank = 6
  _ExportChildren = -> [Binder,DatumPlane,Body]
  _GroupVersion = 1
FEATURE [Part::FeaturePython] Parts  # WARN: FeaturePython — macro-defined, semantics opaque (R4)
  Group = -> [Part,Link,Link001]
  GroupMode = 0
  InvalidShape = false
  TreeRank = 0
  ValidateShape = false
  _LinkVersion = 1
FEATURE [Part::FeaturePython] Assembly  label="Camera_Base_Assembly"  # WARN: FeaturePython — macro-defined, semantics opaque (R4)
  AutoRelax = true
  BuildShape = 0
  Freeze = false
  Group = -> [Constraints,Elements,Parts]
  InvalidShape = false
  TreeRank = 0
  ValidateShape = false
  Verbose = false
  _LinkVersion = 1
  _SolverType = 1
  _Version = 1
FEATURE [App::FeaturePython] Constraints  # WARN: FeaturePython — macro-defined, semantics opaque (R4)
  Group = -> [Constraint,Constraint001]
  TreeRank = 0
  _LinkVersion = 1
  _Version = 1
FEATURE [App::FeaturePython] Elements  # WARN: FeaturePython — macro-defined, semantics opaque (R4)
  Group = -> [Element,Element001,Element002,_Element,_Element001]
  TreeRank = 0
  _LinkVersion = 1
FEATURE [Part::FeaturePython] Element  label="Horn_Base"  # link proxy (typed FeaturePython)
  Detach = false
  InvalidShape = false
  LinkTransform = true
  LinkedObject = -> Link [Body.Pocket.Face4]
  TreeRank = 29
  ValidateShape = false
  _LinkVersion = 1
  _Parent = -> Elements
FEATURE [Part::FeaturePython] Element001  label="MountingHole01"  # link proxy (typed FeaturePython)
  Detach = false
  InvalidShape = false
  LinkTransform = true
  LinkedObject = -> Part [Body.Pocket001.Edge12]
  TreeRank = 35
  ValidateShape = false
  _LinkVersion = 1
  _Parent = -> Elements
FEATURE [Part::FeaturePython] Element002  label="MountingHole02"  # link proxy (typed FeaturePython)
  Detach = false
  InvalidShape = false
  LinkTransform = true
  LinkedObject = -> Part [Body.Pocket001.Edge13]
  TreeRank = 36
  ValidateShape = false
  _LinkVersion = 1
  _Parent = -> Elements
FEATURE [App::FeaturePython] Constraint  label="PlaneCoincident"  # WARN: FeaturePython — macro-defined, semantics opaque (R4)
  Angle = 0
  AnglePitch = 0
  AngleRoll = 0
  Cascade = false
  Disabled = false
  Group = -> [ElementLink,ElementLink001]
  LockAngle = false
  Multiply = false
  OffsetX = 0
  OffsetY = 0
  TreeRank = 41
  _ConstraintType = 35
  _LinkVersion = 1
  _Parent = -> Constraints
FEATURE [App::FeaturePython] ElementLink  label="MountingHole01"  # link proxy (typed FeaturePython)
  LinkTransform = true
  LinkedObject = -> Element001
  TreeRank = 38
  _LinkVersion = 1
  _Parent = -> Constraint
FEATURE [App::FeaturePython] ElementLink001  label="MountingHole01@Link001(Camera_Holder_Assembly)@"  # link proxy (typed FeaturePython)
  LinkTransform = true
  LinkedObject = -> _Element
  TreeRank = 39
  _LinkVersion = 1
  _Parent = -> Constraint
FEATURE [Part::FeaturePython] _Element  label="MountingHole01@Link001(Camera_Holder_Assembly)@"  # link proxy (typed FeaturePython)
  Detach = false
  InvalidShape = false
  LinkTransform = true
  LinkedObject = -> Link001 [1.$MountingHole01.]
  TreeRank = 42
  ValidateShape = false
  _LinkVersion = 1
  _Parent = -> Elements
FEATURE [App::FeaturePython] Constraint001  label="PlaneCoincident001"  # WARN: FeaturePython — macro-defined, semantics opaque (R4)
  Angle = 0
  AnglePitch = 0
  AngleRoll = 0
  Cascade = false
  Disabled = false
  Group = -> [ElementLink002,ElementLink003]
  LockAngle = false
  Multiply = false
  OffsetX = 0
  OffsetY = 0
  TreeRank = 47
  _ConstraintType = 35
  _LinkVersion = 1
  _Parent = -> Constraints
FEATURE [App::FeaturePython] ElementLink002  label="MountingHole02@Link001(Camera_Holder_Assembly)@"  # link proxy (typed FeaturePython)
  LinkTransform = true
  LinkedObject = -> _Element001
  TreeRank = 44
  _LinkVersion = 1
  _Parent = -> Constraint001
FEATURE [Part::FeaturePython] _Element001  label="MountingHole02@Link001(Camera_Holder_Assembly)@"  # link proxy (typed FeaturePython)
  Detach = false
  InvalidShape = false
  LinkTransform = true
  LinkedObject = -> Link001 [1.$MountingHole02.]
  TreeRank = 48
  ValidateShape = false
  _LinkVersion = 1
  _Parent = -> Elements
FEATURE [App::FeaturePython] ElementLink003  label="MountingHole02"  # link proxy (typed FeaturePython)
  LinkTransform = true
  LinkedObject = -> Element002
  TreeRank = 46
  _LinkVersion = 1
  _Parent = -> Constraint001
---- part Top_Base.FCStd = doc fcstd_295a09d94d3a ----
FCSTD DOCUMENT  (FreeCAD 2023.1102R14555 (Git shallow))
Label: Top_Base
License: All rights reserved
LicenseURL: https://en.wikipedia.org/wiki/All_rights_reserved
objects: App::FeaturePython×12, Part::FeaturePython×10, Sketcher::SketchObject×5, PartDesign::Pocket×3, App::Link×2, PartDesign::SubShapeBinder×2, PartDesign::Pad×2, PartDesign::Fillet×1, Part::SubShapeBinder×1, PartDesign::Plane×1, PartDesign::Body×1, App::Part×1
note: 42 computed .brp shape members not serialized (recipe doc carries the construction recipe); baked Part::Feature solids carry a one-line shape summary decoded from their .brp
EXTERNAL_REF file=Servo_Horn.FCStd obj=Part
EXTERNAL_REF file=Hitec_D625MW.FCStd obj=Part

FEATURE [App::Link] Link  label="Link(Servo_Horn)"
  AutoLinkLabel = true
  AutoPlacement = true
  LinkPlacement = pos=(0,0,0) rot=(0.707107,-0.707107,0;3.14159rad)
  LinkedObject = -> <external Servo_Horn.FCStd>#Part
  Placement = pos=(0,0,0) rot=(0.707107,-0.707107,0;3.14159rad)
  SyncGroupVisibility = false
  TreeRank = 1
  _LinkVersion = 1
FEATURE [App::Link] Link001  label="Link001(Hitec_D625MW)"
  AutoLinkLabel = true
  AutoPlacement = true
  LinkPlacement = pos=(40,30,3.99999) rot=(-0.57735,0.57735,0.57735;4.18879rad)
  LinkedObject = -> <external Hitec_D625MW.FCStd>#Part
  Placement = pos=(40,30,3.99999) rot=(-0.57735,0.57735,0.57735;4.18879rad)
  SyncGroupVisibility = false
  TreeRank = 7
  _LinkVersion = 1
FEATURE [PartDesign::SubShapeBinder] Binder  label="Binder(Pocket)"
  BindCopyOnChange = 0
  BindMode = 0
  ClaimChildren = false
  Context = -> Assembly [Parts.Part.Binder.]
  EdgeTolerance = 1e-06
  FillStyle = 0
  Fuse = false
  InvalidShape = false
  MakeFace = true
  MergeEdges = true
  OffsetFill = false
  OffsetIntersection = false
  OffsetJoinType = 0
  OffsetOpenResult = false
  Outline = false
  PartialLoad = false
  Relative = true
  SplitEdges = false
  Support = -> [Link[Body.Pocket.Face9]]
  TightBound = false
  TreeRank = 30
  ValidateShape = false
  _Version = 8
FEATURE [Sketcher::SketchObject] Sketch
  ArcFitTolerance = 1e-06
  AttachmentSupport = -> [Binder]
  ExternalBSplineMaxDegree = 5
  ExternalBSplineTolerance = 0.0001
  ExternalGeometry = -> [Binder]
  FullyConstrained = true
  InternalTolerance = 1e-06
  InvalidShape = false
  MakeInternals = false
  MapMode = 5
  Placement = pos=(0,0,0) rot=(0,1.01411,0;0rad)
  Support = -> [Binder]
  TreeRank = 31
  ValidateShape = false
  sketch-geometry (6):
    g0: GeomPoint [constr] X=0 Y=0 Z=0
    g1: LineSegment StartX=-5.5 StartY=40 StartZ=0 EndX=44.5 EndY=40 EndZ=0
    g2: LineSegment StartX=44.5 StartY=40 StartZ=0 EndX=44.5 EndY=-20 EndZ=0
    g3: LineSegment StartX=44.5 StartY=-20 StartZ=0 EndX=-5.5 EndY=-20 EndZ=0
    g4: LineSegment StartX=-5.5 StartY=-20 StartZ=0 EndX=-5.5 EndY=40 EndZ=0
    g5: GeomPoint [constr] X=-5.5 Y=0 Z=0
  constraints (15):
    c: Coincident(g0,g-1)
    c: Coincident(g1,g2)
    c: Coincident(g2,g3)
    c: Coincident(g3,g4)
    c: Coincident(g4,g1)
    c: Horizontal(g1)
    c: Horizontal(g3)
    c: Vertical(g2)
    c: Distance(g1) = 50
    c: PointOnObject(g5,g-3)
    c: PointOnObject(g5,g-1)
    c: Vertical(g4)
    c: DistanceY(g3,g0) = 20
    c: DistanceY(g0,g1) = 40
    c: PointOnObject(g5,g4)
FEATURE [PartDesign::Pad] Pad
  AddSubType = 0
  AlongSketchNormal = false
  AutoTaperInnerAngle = true
  CheckUpToFaceLimits = true
  ClaimChildren = false
  Direction = (8.74228e-08,-2.3e-15,1)
  Fit = 0
  FitJoin = 0
  InnerFit = 0
  InnerFitJoin = 0
  InvalidShape = false
  Length = 4
  Length2 = 10
  Linearize = true
  NewSolid = false
  Profile = -> Sketch
  ReferenceAxis = -> Sketch [N_Axis]
  Refine = true
  Suppress = false
  TaperInnerAngle = 0
  TaperInnerAngleRev = 0
  TreeRank = 32
  Type = 0
  ValidateShape = true
  _ProfileBasedVersion = 1
FEATURE [PartDesign::Fillet] Fillet
  AddSubType = 0
  Base = -> Pad [Edge8,Edge5,Edge2,Edge1]
  BaseFeature = -> Pad
  InvalidShape = false
  NewSolid = false
  Radius = 4
  Refine = true
  SupportTransform = false
  Suppress = false
  TreeRank = 33
  UseAllEdges = false
  ValidateShape = true
FEATURE [Part::SubShapeBinder] Import  label="Import(Pocket)"
  BindCopyOnChange = 0
  BindMode = 0
  ClaimChildren = false
  Context = -> Assembly [Parts.Part.Body.Import.]
  EdgeTolerance = 1e-06
  FillStyle = 0
  Fuse = false
  InvalidShape = false
  MakeFace = false
  MergeEdges = true
  OffsetFill = false
  OffsetIntersection = false
  OffsetJoinType = 0
  OffsetOpenResult = false
  Outline = false
  PartialLoad = false
  Relative = true
  SplitEdges = false
  Support = -> [Link[Body.Pocket.]]
  TightBound = false
  TreeRank = 36
  ValidateShape = false
  _Version = 8
FEATURE [Sketcher::SketchObject] Sketch001
  ArcFitTolerance = 1e-06
  AttachmentSupport = -> [Fillet]
  ExternalBSplineMaxDegree = 5
  ExternalBSplineTolerance = 0.0001
  ExternalGeometry = -> [Binder,Import]
  FullyConstrained = true
  InternalTolerance = 1e-06
  InvalidShape = false
  MakeInternals = false
  MapMode = 5
  Placement = pos=(3.49691e-07,-9e-15,4) rot=(0,1.01411,0;0rad)
  Support = -> [Fillet]
  TreeRank = 34
  ValidateShape = false
  sketch-geometry (2):
    g0: Circle CenterX=-1.18011e-06 CenterY=7 CenterZ=0 NormalX=0 NormalY=0 NormalZ=1 AngleXU=0 Radius=2.1
    g1: Circle CenterX=1.18011e-06 CenterY=-7 CenterZ=0 NormalX=0 NormalY=0 NormalZ=1 AngleXU=0 Radius=2.1
  constraints (4):
    c: Coincident(g0,g-4)
    c: Coincident(g1,g-3)
    c: Equal(g1,g0)
    c: Diameter(g0) = 4.2
FEATURE [PartDesign::Pocket] Pocket
  AddSubType = 1
  AlongSketchNormal = false
  AutoTaperInnerAngle = true
  BaseFeature = -> Fillet
  CheckUpToFaceLimits = true
  ClaimChildren = false
  Direction = (-8.74228e-08,2.3e-15,-1)
  Fit = 0
  FitJoin = 0
  InnerFit = 0
  InnerFitJoin = 0
  InvalidShape = false
  Length = 5
  Length2 = 10
  Linearize = true
  NewSolid = false
  Profile = -> Sketch001
  ReferenceAxis = -> Sketch001 [N_Axis]
  Refine = true
  Suppress = false
  TaperInnerAngle = 0
  TaperInnerAngleRev = 0
  TreeRank = 35
  Type = 1
  ValidateShape = true
  _ProfileBasedVersion = 1
  _Version = 1
FEATURE [PartDesign::SubShapeBinder] Binder001  label="Binder001(*Hitec_D625MW)"
  BindCopyOnChange = 0
  BindMode = 0
  ClaimChildren = false
  Context = -> Assembly [Parts.Part.Body.Binder001.]
  EdgeTolerance = 1e-06
  FillStyle = 0
  Fuse = false
  InvalidShape = false
  MakeFace = true
  MergeEdges = true
  OffsetFill = false
  OffsetIntersection = false
  OffsetJoinType = 0
  OffsetOpenResult = false
  Outline = false
  PartialLoad = false
  Relative = true
  SplitEdges = false
  Support = -> [Link001]
  TightBound = false
  TreeRank = 61
  ValidateShape = false
  _Version = 8
FEATURE [Sketcher::SketchObject] Sketch002
  ArcFitTolerance = 1e-06
  AttachmentSupport = -> [Pocket]
  ExternalBSplineMaxDegree = 5
  ExternalBSplineTolerance = 0.0001
  ExternalGeometry = -> [Binder001]
  FullyConstrained = true
  InternalTolerance = 1e-06
  InvalidShape = false
  MakeInternals = false
  MapMode = 5
  Placement = pos=(3.49691e-07,-9e-15,4) rot=(0,1.01411,0;0rad)
  Support = -> [Pocket]
  TreeRank = 62
  ValidateShape = false
  sketch-geometry (12):
    g0: LineSegment StartX=2.5 StartY=-11.1 StartZ=0 EndX=10.5 EndY=-11.1 EndZ=0
    g1: LineSegment StartX=11.5 StartY=-18.7 StartZ=0 EndX=2.5 EndY=-18.7 EndZ=0
    g2: LineSegment StartX=2.5 StartY=-18.7 StartZ=0 EndX=2.5 EndY=-11.1 EndZ=0
    g3: LineSegment StartX=2.50001 StartY=38.1 StartZ=0 EndX=11.5 EndY=38.1 EndZ=0
    g4: LineSegment StartX=10.5 StartY=30.5 StartZ=0 EndX=2.50001 EndY=30.5 EndZ=0
    g5: LineSegment StartX=2.50001 StartY=30.5 StartZ=0 EndX=2.50001 EndY=38.1 EndZ=0
    g6: LineSegment StartX=10.5 StartY=-11.1 StartZ=0 EndX=10.5 EndY=-17.2 EndZ=0
    g7: LineSegment StartX=10.5 StartY=-17.2 StartZ=0 EndX=11.5 EndY=-17.2 EndZ=0
    g8: LineSegment StartX=11.5 StartY=-17.2 StartZ=0 EndX=11.5 EndY=-18.7 EndZ=0
    g9: LineSegment StartX=10.5 StartY=36.6 StartZ=0 EndX=10.5 EndY=30.5 EndZ=0
    g10: LineSegment StartX=10.5 StartY=36.6 StartZ=0 EndX=11.5 EndY=36.6 EndZ=0
    g11: LineSegment StartX=11.5 StartY=36.6 StartZ=0 EndX=11.5 EndY=38.1 EndZ=0
  constraints (36):
    c: Coincident(g0,g6)
    c: Coincident(g1,g2)
    c: Coincident(g2,g0)
    c: Horizontal(g0)
    c: Horizontal(g1)
    c: Vertical(g2)
    c: Coincident(g9,g4)
    c: Coincident(g4,g5)
    c: Coincident(g5,g3)
    c: Horizontal(g3)
    c: Horizontal(g4)
    c: Vertical(g5)
    c: Equal(g2,g5)
    c: Equal(g3,g1)
    c: Distance(g-7,g0) = 0.5
    c: Distance(g-8,g4) = 0.5
    c: Vertical(g6)
    c: PointOnObject(g-3,g6)
    c: Coincident(g7,g6)
    c: Horizontal(g7)
    c: Coincident(g8,g7)
    c: Vertical(g8)
    c: Coincident(g1,g8)
    c: Distance(g6,g-4) = 0.1
    c: Distance(g7) = 1
    c: Vertical(g9)
    c: Coincident(g10,g9)
    c: Horizontal(g10)
    c: Coincident(g11,g10)
    c: Vertical(g11)
    c: Coincident(g3,g11)
    c: Equal(g10,g7)
    c: PointOnObject(g-5,g9)
    c: Equal(g6,g9)
    c: Distance(g8) = 1.5
    c: Distance(g0) = 8
FEATURE [PartDesign::Pad] Pad001
  AddSubType = 0
  AlongSketchNormal = false
  AutoTaperInnerAngle = true
  BaseFeature = -> Pocket
  CheckUpToFaceLimits = true
  ClaimChildren = false
  Direction = (8.74228e-08,-2.3e-15,1)
  Fit = 0
  FitJoin = 0
  InnerFit = 0
  InnerFitJoin = 0
  InvalidShape = false
  Length = 10
  Length2 = 10
  Linearize = true
  NewSolid = false
  Profile = -> Sketch002
  ReferenceAxis = -> Sketch002 [N_Axis]
  Refine = true
  Suppress = false
  TaperInnerAngle = 0
  TaperInnerAngleRev = 0
  TreeRank = 63
  Type = 3
  UpToFace = -> Binder001 [Face10]
  ValidateShape = true
  _ProfileBasedVersion = 1
FEATURE [PartDesign::Plane] DatumPlane
  AttachmentSupport = -> [Pad001]
  InvalidShape = false
  Length = 13.9
  MapMode = 45
  MinimumLength = 10
  MinimumWidth = 10
  Placement = pos=(10.5,9.7,13.9) rot=(0.707107,0,0.707107;3.14159rad)
  ResizeMode = 0
  Support = -> [Pad001]
  TreeRank = 64
  ValidateShape = false
  Width = 18.8
FEATURE [Sketcher::SketchObject] Sketch003
  ArcFitTolerance = 1e-06
  AttachmentSupport = -> [DatumPlane]
  ExternalBSplineMaxDegree = 5
  ExternalBSplineTolerance = 0.0001
  ExternalGeometry = -> [Binder001]
  FullyConstrained = true
  InternalTolerance = 1e-06
  InvalidShape = false
  MakeInternals = false
  MapMode = 5
  Placement = pos=(10.5,9.7,13.9) rot=(0.707107,0,0.707107;3.14159rad)
  Support = -> [DatumPlane]
  TreeRank = 65
  ValidateShape = false
  sketch-geometry (4):
    g0: Circle CenterX=5.1 CenterY=24.2 CenterZ=0 NormalX=0 NormalY=0 NormalZ=1 AngleXU=0 Radius=2.4
    g1: Circle CenterX=-5.1 CenterY=24.2 CenterZ=0 NormalX=0 NormalY=0 NormalZ=1 AngleXU=0 Radius=2.4
    g2: Circle CenterX=5.1 CenterY=-24.2 CenterZ=0 NormalX=0 NormalY=0 NormalZ=1 AngleXU=0 Radius=2.4
    g3: Circle CenterX=-5.1 CenterY=-24.2 CenterZ=0 NormalX=0 NormalY=0 NormalZ=1 AngleXU=0 Radius=2.4
  constraints (8):
    c: Coincident(g0,g-5)
    c: Coincident(g1,g-6)
    c: Coincident(g2,g-3)
    c: Coincident(g3,g-4)
    c: Equal(g3,g2)
    c: Equal(g2,g0)
    c: Equal(g0,g1)
    c: Diameter(g0) = 4.8
FEATURE [PartDesign::Pocket] Pocket001
  AddSubType = 1
  AlongSketchNormal = false
  AutoTaperInnerAngle = true
  BaseFeature = -> Pad001
  CheckUpToFaceLimits = true
  ClaimChildren = false
  Direction = (-1,1.76265e-07,8.74228e-08)
  Fit = 0
  FitJoin = 0
  InnerFit = 0
  InnerFitJoin = 0
  InvalidShape = false
  Length = 5
  Length2 = 10
  Linearize = true
  Midplane = true
  NewSolid = false
  Profile = -> Sketch003
  ReferenceAxis = -> Sketch003 [N_Axis]
  Refine = true
  Suppress = false
  TaperInnerAngle = 0
  TaperInnerAngleRev = 0
  TreeRank = 66
  Type = 1
  ValidateShape = true
  _ProfileBasedVersion = 1
  _Version = 1
FEATURE [Sketcher::SketchObject] Sketch004
  ArcFitTolerance = 1e-06
  AttachmentSupport = -> [DatumPlane]
  ExternalBSplineMaxDegree = 5
  ExternalBSplineTolerance = 0.0001
  ExternalGeometry = -> [Binder001,Pocket001]
  FullyConstrained = true
  InternalTolerance = 1e-06
  InvalidShape = false
  MakeInternals = false
  MapMode = 5
  Placement = pos=(10.5,9.7,13.9) rot=(0.707107,0,0.707107;3.14159rad)
  Support = -> [DatumPlane]
  TreeRank = 67
  ValidateShape = false
  sketch-geometry (8):
    g0: LineSegment StartX=0.8 StartY=26.9 StartZ=0 EndX=-0.8 EndY=26.9 EndZ=0
    g1: LineSegment StartX=-0.8 StartY=26.9 StartZ=0 EndX=-0.8 EndY=20.8 EndZ=0
    g2: LineSegment StartX=-0.8 StartY=20.8 StartZ=0 EndX=0.8 EndY=20.8 EndZ=0
    g3: LineSegment StartX=0.8 StartY=20.8 StartZ=0 EndX=0.8 EndY=26.9 EndZ=0
    g4: LineSegment StartX=0.8 StartY=-20.8 StartZ=0 EndX=-0.8 EndY=-20.8 EndZ=0
    g5: LineSegment StartX=-0.8 StartY=-20.8 StartZ=0 EndX=-0.8 EndY=-26.9 EndZ=0
    g6: LineSegment StartX=-0.8 StartY=-26.9 StartZ=0 EndX=0.8 EndY=-26.9 EndZ=0
    g7: LineSegment StartX=0.8 StartY=-26.9 StartZ=0 EndX=0.8 EndY=-20.8 EndZ=0
  constraints (22):
    c: Coincident(g0,g1)
    c: Coincident(g1,g2)
    c: Coincident(g2,g3)
    c: Coincident(g3,g0)
    c: Horizontal(g2)
    c: Vertical(g1)
    c: Vertical(g3)
    c: PointOnObject(g0,g-9)
    c: PointOnObject(g1,g-7)
    c: Symmetric(g0,g0,g-2)
    c: Distance(g-5,g3) = 0.2
    c: Coincident(g4,g5)
    c: Coincident(g5,g6)
    c: Coincident(g6,g7)
    c: Coincident(g7,g4)
    c: Horizontal(g4)
    c: Vertical(g5)
    c: Vertical(g7)
    c: PointOnObject(g4,g-8)
    c: PointOnObject(g5,g-10)
    c: Symmetric(g5,g6,g-2)
    c: Distance(g-3,g7) = 0.2
FEATURE [PartDesign::Pocket] Pocket002
  AddSubType = 1
  AlongSketchNormal = false
  AutoTaperInnerAngle = true
  BaseFeature = -> Pocket001
  CheckUpToFaceLimits = true
  ClaimChildren = false
  Direction = (-1,1.76265e-07,8.74228e-08)
  Fit = 0
  FitJoin = 0
  InnerFit = 0
  InnerFitJoin = 0
  InvalidShape = false
  Length = 4
  Length2 = 10
  Linearize = true
  Midplane = true
  NewSolid = false
  Profile = -> Sketch004
  ReferenceAxis = -> Sketch004 [N_Axis]
  Refine = true
  Suppress = false
  TaperInnerAngle = 0
  TaperInnerAngleRev = 0
  TreeRank = 68
  Type = 0
  ValidateShape = true
  _ProfileBasedVersion = 1
  _Version = 1
FEATURE [PartDesign::Body] Body
  AutoGroupSolids = false
  ClaimAllChildren = false
  ExportMode = 0
  Group = -> [Binder,Sketch,Pad,Fillet,Sketch001,Pocket,Import,Binder001,Sketch002,Pad001,DatumPlane,Sketch003,Pocket001,Sketch004,Pocket002]
  InvalidShape = false
  Origin = -> Origin001
  Tip = -> Pocket002
  TreeRank = 29
  ValidateShape = false
  _ExportChildren = -> [Binder,Pad,Fillet,Pocket,Import,Binder001,Pad001,DatumPlane,Pocket001,Pocket002]
  _GroupVersion = 1
FEATURE [App::Part] Part  label="Top_Base"
  ClaimAllChildren = false
  ExportMode = 1
  Group = -> [Body]
  Origin = -> Origin
  Placement = pos=(5.99042e-09,9.86e-14,-3.642e-13) rot=(0,0.463815,0.889887;0rad)
  TreeRank = 17
  _ExportChildren = -> [Body]
  _GroupVersion = 1
FEATURE [Part::FeaturePython] Parts  # WARN: FeaturePython — macro-defined, semantics opaque (R4)
  Group = -> [Part,Link,Link001]
  GroupMode = 0
  InvalidShape = false
  TreeRank = 5
  ValidateShape = false
  _LinkVersion = 1
FEATURE [Part::FeaturePython] Assembly  label="Top_Base_Assembly"  # WARN: FeaturePython — macro-defined, semantics opaque (R4)
  AutoRelax = true
  BuildShape = 0
  Freeze = false
  Group = -> [Constraints,Elements,Parts]
  InvalidShape = false
  TreeRank = 6
  ValidateShape = false
  Verbose = false
  _LinkVersion = 1
  _SolverType = 1
  _Version = 1
FEATURE [App::FeaturePython] Constraints  # WARN: FeaturePython — macro-defined, semantics opaque (R4)
  Group = -> [Constraint,Constraint001,Constraint002,Constraint004]
  TreeRank = 3
  _LinkVersion = 1
  _Version = 1
FEATURE [App::FeaturePython] Elements  # WARN: FeaturePython — macro-defined, semantics opaque (R4)
  Group = -> [_Element,_Element001,_Element002,_Element003,_Element004,_Element005,_Element006,Element]
  TreeRank = 4
  _LinkVersion = 1
FEATURE [App::FeaturePython] Constraint  label="Locked"  # WARN: FeaturePython — macro-defined, semantics opaque (R4)
  Disabled = false
  Group = -> [ElementLink]
  TreeRank = 11
  _ConstraintType = 0
  _LinkVersion = 1
  _Parent = -> Constraints
FEATURE [App::FeaturePython] ElementLink  label="_Element"  # link proxy (typed FeaturePython)
  LinkTransform = true
  LinkedObject = -> _Element
  TreeRank = 9
  _LinkVersion = 1
  _Parent = -> Constraint
FEATURE [Part::FeaturePython] _Element  # link proxy (typed FeaturePython)
  Detach = false
  InvalidShape = false
  LinkTransform = true
  LinkedObject = -> Link [Body.Pocket.Face4]
  TreeRank = 12
  ValidateShape = false
  _LinkVersion = 1
  _Parent = -> Elements
FEATURE [App::FeaturePython] Constraint001  label="PlaneCoincident"  # WARN: FeaturePython — macro-defined, semantics opaque (R4)
  Angle = 0
  AnglePitch = 0
  AngleRoll = 0
  Cascade = false
  Disabled = false
  Group = -> [ElementLink001,ElementLink002]
  LockAngle = false
  Multiply = false
  OffsetX = 0
  OffsetY = 0
  TreeRank = 42
  _ConstraintType = 35
  _LinkVersion = 1
  _Parent = -> Constraints
FEATURE [App::FeaturePython] ElementLink001  label="_Element001"  # link proxy (typed FeaturePython)
  LinkTransform = true
  LinkedObject = -> _Element001
  TreeRank = 38
  _LinkVersion = 1
  _Parent = -> Constraint001
FEATURE [Part::FeaturePython] _Element001  # link proxy (typed FeaturePython)
  Detach = false
  InvalidShape = false
  LinkTransform = true
  LinkedObject = -> Link [Body.Pocket.Edge14]
  TreeRank = 43
  ValidateShape = false
  _LinkVersion = 1
  _Parent = -> Elements
FEATURE [App::FeaturePython] ElementLink002  label="_Element002"  # link proxy (typed FeaturePython)
  LinkTransform = true
  LinkedObject = -> _Element002
  TreeRank = 40
  _LinkVersion = 1
  _Parent = -> Constraint001
FEATURE [Part::FeaturePython] _Element002  # link proxy (typed FeaturePython)
  Detach = false
  InvalidShape = false
  LinkTransform = true
  LinkedObject = -> Part [Body.Pocket.Edge12]
  TreeRank = 44
  ValidateShape = false
  _LinkVersion = 1
  _Parent = -> Elements
FEATURE [App::FeaturePython] Constraint002  label="PlaneCoincident001"  # WARN: FeaturePython — macro-defined, semantics opaque (R4)
  Angle = 0
  AnglePitch = 0
  AngleRoll = 0
  Cascade = false
  Disabled = false
  Group = -> [ElementLink003,ElementLink004]
  LockAngle = false
  Multiply = false
  OffsetX = 0
  OffsetY = 0
  TreeRank = 50
  _ConstraintType = 35
  _LinkVersion = 1
  _Parent = -> Constraints
FEATURE [App::FeaturePython] ElementLink003  label="_Element003"  # link proxy (typed FeaturePython)
  LinkTransform = true
  LinkedObject = -> _Element003
  TreeRank = 46
  _LinkVersion = 1
  _Parent = -> Constraint002
FEATURE [Part::FeaturePython] _Element003  # link proxy (typed FeaturePython)
  Detach = false
  InvalidShape = false
  LinkTransform = true
  LinkedObject = -> Part [Body.Pocket.Edge14]
  TreeRank = 51
  ValidateShape = false
  _LinkVersion = 1
  _Parent = -> Elements
FEATURE [App::FeaturePython] ElementLink004  label="_Element004"  # link proxy (typed FeaturePython)
  LinkTransform = true
  LinkedObject = -> _Element004
  TreeRank = 48
  _LinkVersion = 1
  _Parent = -> Constraint002
FEATURE [Part::FeaturePython] _Element004  # link proxy (typed FeaturePython)
  Detach = false
  InvalidShape = false
  LinkTransform = true
  LinkedObject = -> Link [Body.Pocket.Edge31]
  TreeRank = 52
  ValidateShape = false
  _LinkVersion = 1
  _Parent = -> Elements
FEATURE [Part::FeaturePython] _Element005  # link proxy (typed FeaturePython)
  Detach = false
  InvalidShape = false
  LinkTransform = true
  LinkedObject = -> Part [Body.Pocket.Face5]
  TreeRank = 59
  ValidateShape = false
  _LinkVersion = 1
  _Parent = -> Elements
FEATURE [Part::FeaturePython] _Element006  # link proxy (typed FeaturePython)
  Detach = false
  InvalidShape = false
  LinkTransform = true
  LinkedObject = -> Link001 [Body.Fillet.Face17]
  TreeRank = 60
  ValidateShape = false
  _LinkVersion = 1
  _Parent = -> Elements
FEATURE [App::FeaturePython] Constraint004  label="Locked001"  # WARN: FeaturePython — macro-defined, semantics opaque (R4)
  Disabled = false
  Group = -> [ElementLink007]
  TreeRank = 72
  _ConstraintType = 0
  _LinkVersion = 1
  _Parent = -> Constraints
FEATURE [App::FeaturePython] ElementLink007  label="_Element006"  # link proxy (typed FeaturePython)
  LinkTransform = true
  LinkedObject = -> _Element006
  TreeRank = 71
  _LinkVersion = 1
  _Parent = -> Constraint004
FEATURE [Part::FeaturePython] Element  label="Servo_Gear_Base"  # link proxy (typed FeaturePython)
  Detach = false
  InvalidShape = false
  LinkTransform = true
  LinkedObject = -> Link001 [Body.Fillet.Face63]
  TreeRank = 73
  ValidateShape = false
  _LinkVersion = 1
  _Parent = -> Elements
